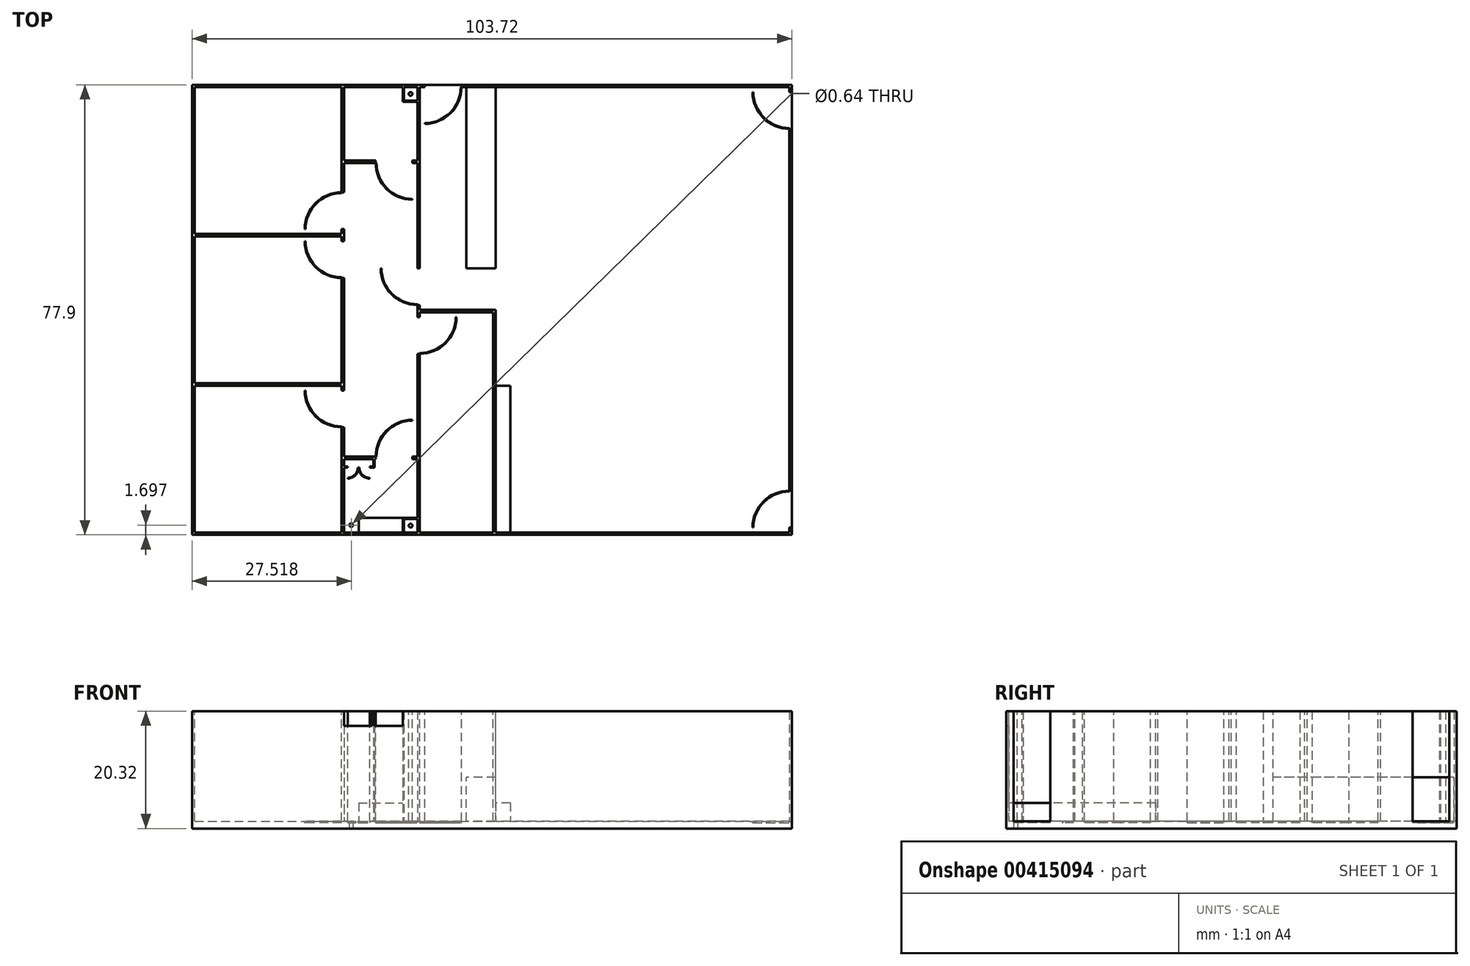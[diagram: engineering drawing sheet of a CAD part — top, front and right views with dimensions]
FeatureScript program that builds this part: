
annotation { "Feature Type Name" : "Feature", "Feature Type Description" : "" }
export const myFeature = defineFeature(function(context is Context, id is Id, definition is map)
    precondition{}
    {
        {
            var Q0;
            Q0=qCreatedBy(makeId("Top.planeOp"),FACE);
            var sketch = newSketch(context, id + "F0", { "sketchPlane" : qUnion([Q0])});
            skLineSegment(sketch, "E0.bottom", {"start": v(51.86, 38.95) * mm, "end": v(-51.86, 38.95) * mm});
            skLineSegment(sketch, "E0.top", {"start": v(51.86, -38.95) * mm, "end": v(-51.86, -38.95) * mm});
            skLineSegment(sketch, "E0.left", {"start": v(51.86, 38.95) * mm, "end": v(51.86, -38.95) * mm});
            skLineSegment(sketch, "E0.right", {"start": v(-51.86, 38.95) * mm, "end": v(-51.86, -38.95) * mm});
            skPoint(sketch, "E0.middle", {"position": v(0, 0) * mm});
            skSolve(sketch);
        }
        {
            var Q0;
            Q0 = qSketchRegion(id + "F0", true);
            extrude(context, id + "F1", {"entities" : qUnion([Q0]), "depth" : 20.32 * mm});
        }
        {
            var Q0;
            Q0=makeQuery(id+"F1.opExtrude","CAP_FACE",FACE,{"disambiguationData":[OSD([sQuery(id+"F0.wireOp",EDGE,"E0.bottom"),sQuery(id+"F0.wireOp",EDGE,"E0.top"),sQuery(id+"F0.wireOp",EDGE,"E0.left"),sQuery(id+"F0.wireOp",EDGE,"E0.right")])],"isStart":false});
            var sketch = newSketch(context, id + "F2", { "sketchPlane" : qUnion([Q0])});
            skLineSegment(sketch, "E1.bottom", {"start": v(-51.43, 38.52) * mm, "end": v(-26.03, 38.52) * mm});
            skLineSegment(sketch, "E1.top", {"start": v(-51.43, 13.12) * mm, "end": v(-26.03, 13.12) * mm});
            skLineSegment(sketch, "E1.left", {"start": v(-51.43, 38.52) * mm, "end": v(-51.43, 13.12) * mm});
            skLineSegment(sketch, "E1.right", {"start": v(-26.03, 38.52) * mm, "end": v(-26.03, 13.12) * mm});
            skLineSegment(sketch, "E2.bottom", {"start": v(-51.43, 12.7) * mm, "end": v(-26.03, 12.7) * mm});
            skLineSegment(sketch, "E2.top", {"start": v(-51.43, -12.7) * mm, "end": v(-26.03, -12.7) * mm});
            skLineSegment(sketch, "E2.left", {"start": v(-51.43, 12.7) * mm, "end": v(-51.43, -12.7) * mm});
            skLineSegment(sketch, "E2.right", {"start": v(-26.03, 12.7) * mm, "end": v(-26.03, -12.7) * mm});
            skLineSegment(sketch, "E3.bottom", {"start": v(-51.43, -13.12) * mm, "end": v(-26.03, -13.12) * mm});
            skLineSegment(sketch, "E3.top", {"start": v(-51.43, -38.52) * mm, "end": v(-26.03, -38.52) * mm});
            skLineSegment(sketch, "E3.left", {"start": v(-51.43, -13.12) * mm, "end": v(-51.43, -38.52) * mm});
            skLineSegment(sketch, "E3.right", {"start": v(-26.03, -13.12) * mm, "end": v(-26.03, -38.52) * mm});
            skLineSegment(sketch, "E4.bottom", {"start": v(-25.61, -25.82) * mm, "end": v(-12.91, -25.82) * mm});
            skLineSegment(sketch, "E4.top", {"start": v(-25.61, -38.52) * mm, "end": v(-12.91, -38.52) * mm});
            skLineSegment(sketch, "E4.left", {"start": v(-25.61, -25.82) * mm, "end": v(-25.61, -38.52) * mm});
            skLineSegment(sketch, "E4.right", {"start": v(-12.91, -25.82) * mm, "end": v(-12.91, -38.52) * mm});
            skLineSegment(sketch, "E5.bottom", {"start": v(-25.61, 38.52) * mm, "end": v(-12.91, 38.52) * mm});
            skLineSegment(sketch, "E5.top", {"start": v(-25.61, 25.82) * mm, "end": v(-12.91, 25.82) * mm});
            skLineSegment(sketch, "E5.left", {"start": v(-25.61, 38.52) * mm, "end": v(-25.61, 25.82) * mm});
            skLineSegment(sketch, "E5.right", {"start": v(-12.91, 38.52) * mm, "end": v(-12.91, 25.82) * mm});
            skLineSegment(sketch, "E6", {"start": v(-25.61, 25.82) * mm, "end": v(-25.61, -25.82) * mm});
            skLineSegment(sketch, "E7.bottom", {"start": v(-12.49, 0) * mm, "end": v(0.64, 0) * mm});
            skLineSegment(sketch, "E7.top", {"start": v(-12.49, -38.52) * mm, "end": v(0.64, -38.52) * mm});
            skLineSegment(sketch, "E7.left", {"start": v(-12.49, 0) * mm, "end": v(-12.49, -38.52) * mm});
            skLineSegment(sketch, "E7.right", {"start": v(0.64, 0) * mm, "end": v(0.64, -38.52) * mm});
            skLineSegment(sketch, "E8", {"start": v(-12.49, 38.52) * mm, "end": v(-12.49, 7.2) * mm});
            skLineSegment(sketch, "E9", {"start": v(-12.91, 25.82) * mm, "end": v(-12.91, 7.2) * mm});
            skLineSegment(sketch, "E10", {"start": v(-12.91, 7.2) * mm, "end": v(-12.49, 7.2) * mm});
            skLineSegment(sketch, "E11", {"start": v(-12.91, -25.82) * mm, "end": v(-12.91, 0) * mm});
            skLineSegment(sketch, "E12", {"start": v(-12.91, 0) * mm, "end": v(-12.49, 0) * mm});
            skLineSegment(sketch, "E13.bottom", {"start": v(0.64, 38.52) * mm, "end": v(-4.44, 38.52) * mm});
            skLineSegment(sketch, "E13.top", {"start": v(0.64, 7.2) * mm, "end": v(-4.44, 7.2) * mm});
            skLineSegment(sketch, "E13.left", {"start": v(0.64, 38.52) * mm, "end": v(0.64, 7.2) * mm});
            skLineSegment(sketch, "E13.right", {"start": v(-4.44, 38.52) * mm, "end": v(-4.44, 7.2) * mm});
            skLineSegment(sketch, "E14", {"start": v(-12.49, 38.52) * mm, "end": v(51.43, 38.52) * mm});
            skLineSegment(sketch, "E15", {"start": v(-25.61, 25.4) * mm, "end": v(-12.91, 25.4) * mm});
            skLineSegment(sketch, "E16", {"start": v(-25.61, -25.4) * mm, "end": v(-12.91, -25.4) * mm});
            skLineSegment(sketch, "E17", {"start": v(-12.49, -0.42) * mm, "end": v(0.21, -0.42) * mm});
            skLineSegment(sketch, "E18", {"start": v(0.21, -0.42) * mm, "end": v(0.21, -38.52) * mm});
            skLineSegment(sketch, "E19", {"start": v(51.43, 38.52) * mm, "end": v(51.43, -38.52) * mm});
            skLineSegment(sketch, "E20", {"start": v(51.43, -38.52) * mm, "end": v(0.64, -38.52) * mm});
            skLineSegment(sketch, "E21", {"start": v(-12.91, 0.85) * mm, "end": v(-12.49, 0.85) * mm});
            skLineSegment(sketch, "E22", {"start": v(-12.49, 0.85) * mm, "end": v(-12.49, 0) * mm});
            skLineSegment(sketch, "E23", {"start": v(-12.91, 0.85) * mm, "end": v(-12.91, 0) * mm});
            skSolve(sketch);
        }
        {
            var Q0;
            Q0=makeQuery(id+"F2.imprint","IMPRINT",FACE,{"disambiguationData":[TD([[makeQuery(id+"F2.imprint","IMPRINT",EDGE,{"derivedFrom":sQuery(id+"F2.wireOp",EDGE,"E7.bottom")}),1.0]])]});
            var Q1;
            {var subQ4=sQuery(id+"F2.wireOp",EDGE,"E17");Q1=makeQuery(id+"F2.imprint","IMPRINT",FACE,{"disambiguationData":[TD([[makeQuery(id+"F2.imprint","IMPRINT",EDGE,{"derivedFrom":subQ4}),-1.0]])]});}
            var Q2;
            Q2=makeQuery(id+"F2.imprint","IMPRINT",FACE,{"disambiguationData":[TD([[makeQuery(id+"F2.imprint","IMPRINT",EDGE,{"derivedFrom":sQuery(id+"F2.wireOp",EDGE,"E5.bottom")}),-1.0]])]});
            var Q3;
            Q3=makeQuery(id+"F2.imprint","IMPRINT",FACE,{"disambiguationData":[TD([[makeQuery(id+"F2.imprint","IMPRINT",EDGE,{"derivedFrom":sQuery(id+"F2.wireOp",EDGE,"E1.bottom")}),-1.0]])]});
            var Q4;
            Q4=makeQuery(id+"F2.imprint","IMPRINT",FACE,{"disambiguationData":[TD([[makeQuery(id+"F2.imprint","IMPRINT",EDGE,{"derivedFrom":sQuery(id+"F2.wireOp",EDGE,"E2.bottom")}),-1.0]])]});
            var Q5;
            Q5=makeQuery(id+"F2.imprint","IMPRINT",FACE,{"disambiguationData":[TD([[makeQuery(id+"F2.imprint","IMPRINT",EDGE,{"derivedFrom":sQuery(id+"F2.wireOp",EDGE,"E3.bottom")}),-1.0]])]});
            var Q6;
            Q6=makeQuery(id+"F2.imprint","IMPRINT",FACE,{"disambiguationData":[TD([[makeQuery(id+"F2.imprint","IMPRINT",EDGE,{"derivedFrom":sQuery(id+"F2.wireOp",EDGE,"E4.bottom")}),-1.0]])]});
            extrude(context, id + "F3", {"entities" : qUnion([Q0, Q1, Q2, Q3, Q4, Q5, Q6]), "operationType" : NewBodyOperationType.REMOVE, "oppositeDirection" : true, "depth" : 19.05 * mm});
        }
        {
            var Q0;
            Q0=makeQuery(id+"F2.imprint","IMPRINT",FACE,{"disambiguationData":[TD([[makeQuery(id+"F2.imprint","IMPRINT",EDGE,{"derivedFrom":sQuery(id+"F2.wireOp",EDGE,"E13.top")}),-1.0]])]});
            extrude(context, id + "F4", {"entities" : qUnion([Q0]), "operationType" : NewBodyOperationType.REMOVE, "oppositeDirection" : true, "depth" : 11.43 * mm});
        }
        {
            var Q0;
            Q0=makeQuery(id+"F3.boolean.opBoolean","COPY",FACE,{"derivedFrom":makeQuery(id+"F3.opExtrude","CAP_FACE",FACE,{"disambiguationData":[OSD([sQuery(id+"F2.wireOp",EDGE,"E6"),sQuery(id+"F2.wireOp",EDGE,"E7.bottom"),sQuery(id+"F2.wireOp",EDGE,"E7.right"),sQuery(id+"F2.wireOp",EDGE,"E8"),sQuery(id+"F2.wireOp",EDGE,"E9"),sQuery(id+"F2.wireOp",EDGE,"E10"),sQuery(id+"F2.wireOp",EDGE,"E11"),sQuery(id+"F2.wireOp",EDGE,"E12"),sQuery(id+"F2.wireOp",EDGE,"E13.top"),sQuery(id+"F2.wireOp",EDGE,"E13.left"),sQuery(id+"F2.wireOp",EDGE,"E13.right"),sQuery(id+"F2.wireOp",EDGE,"E14"),sQuery(id+"F2.wireOp",EDGE,"E15"),sQuery(id+"F2.wireOp",EDGE,"E16"),sQuery(id+"F2.wireOp",EDGE,"E19"),sQuery(id+"F2.wireOp",EDGE,"E20")])],"isStart":false})});
            var sketch = newSketch(context, id + "F5", { "sketchPlane" : qUnion([Q0])});
            skLineSegment(sketch, "E24.bottom", {"start": v(-14.34, -7.62) * mm, "end": v(-3.56, -7.62) * mm});
            skLineSegment(sketch, "E24.top", {"start": v(-14.34, -1.27) * mm, "end": v(-3.56, -1.27) * mm});
            skLineSegment(sketch, "E24.left", {"start": v(-14.34, -7.62) * mm, "end": v(-14.34, -1.27) * mm});
            skLineSegment(sketch, "E24.right", {"start": v(-3.56, -7.62) * mm, "end": v(-3.56, -1.27) * mm});
            skLineSegment(sketch, "E25.bottom", {"start": v(-24.44, -13.97) * mm, "end": v(-32.91, -13.97) * mm});
            skLineSegment(sketch, "E25.top", {"start": v(-24.44, -20.32) * mm, "end": v(-32.91, -20.32) * mm});
            skLineSegment(sketch, "E25.left", {"start": v(-24.44, -13.97) * mm, "end": v(-24.44, -20.32) * mm});
            skLineSegment(sketch, "E25.right", {"start": v(-32.91, -13.97) * mm, "end": v(-32.91, -20.32) * mm});
            skLineSegment(sketch, "E26.bottom", {"start": v(-33.22, 13.97) * mm, "end": v(-23.28, 13.97) * mm});
            skLineSegment(sketch, "E26.top", {"start": v(-33.22, 20.32) * mm, "end": v(-23.28, 20.32) * mm});
            skLineSegment(sketch, "E26.left", {"start": v(-33.22, 13.97) * mm, "end": v(-33.22, 20.32) * mm});
            skLineSegment(sketch, "E26.right", {"start": v(-23.28, 13.97) * mm, "end": v(-23.28, 20.32) * mm});
            skLineSegment(sketch, "E27.bottom", {"start": v(-33.63, 11.85) * mm, "end": v(-25.61, 11.85) * mm});
            skLineSegment(sketch, "E27.top", {"start": v(-33.63, 5.5) * mm, "end": v(-25.61, 5.5) * mm});
            skLineSegment(sketch, "E27.left", {"start": v(-33.63, 11.85) * mm, "end": v(-33.63, 5.5) * mm});
            skLineSegment(sketch, "E27.right", {"start": v(-25.61, 11.85) * mm, "end": v(-25.61, 5.5) * mm});
            skLineSegment(sketch, "E28.bottom", {"start": v(-20.1, 28.26) * mm, "end": v(-13.76, 28.26) * mm});
            skLineSegment(sketch, "E28.top", {"start": v(-20.1, 22.28) * mm, "end": v(-13.76, 22.28) * mm});
            skLineSegment(sketch, "E28.left", {"start": v(-20.1, 28.26) * mm, "end": v(-20.1, 22.28) * mm});
            skLineSegment(sketch, "E28.right", {"start": v(-13.76, 28.26) * mm, "end": v(-13.76, 22.28) * mm});
            skLineSegment(sketch, "E29.bottom", {"start": v(-20.1, -22.33) * mm, "end": v(-13.76, -22.33) * mm});
            skLineSegment(sketch, "E29.top", {"start": v(-20.1, -29.4) * mm, "end": v(-13.76, -29.4) * mm});
            skLineSegment(sketch, "E29.left", {"start": v(-20.1, -22.33) * mm, "end": v(-20.1, -29.4) * mm});
            skLineSegment(sketch, "E29.right", {"start": v(-13.76, -22.33) * mm, "end": v(-13.76, -29.4) * mm});
            skLineSegment(sketch, "E30.bottom", {"start": v(41.47, 37.68) * mm, "end": v(56, 37.68) * mm});
            skLineSegment(sketch, "E30.top", {"start": v(41.47, 31.33) * mm, "end": v(56, 31.33) * mm});
            skLineSegment(sketch, "E30.left", {"start": v(41.47, 37.68) * mm, "end": v(41.47, 31.33) * mm});
            skLineSegment(sketch, "E30.right", {"start": v(56, 37.68) * mm, "end": v(56, 31.33) * mm});
            skLineSegment(sketch, "E31.bottom", {"start": v(42.78, -31.33) * mm, "end": v(59.87, -31.33) * mm});
            skLineSegment(sketch, "E31.top", {"start": v(42.78, -37.68) * mm, "end": v(59.87, -37.68) * mm});
            skLineSegment(sketch, "E31.left", {"start": v(42.78, -31.33) * mm, "end": v(42.78, -37.68) * mm});
            skLineSegment(sketch, "E31.right", {"start": v(59.87, -31.33) * mm, "end": v(59.87, -37.68) * mm});
            skSolve(sketch);
        }
        {
            var Q0;
            Q0 = qSketchRegion(id + "F5", true);
            extrude(context, id + "F6", {"entities" : qUnion([Q0]), "operationType" : NewBodyOperationType.REMOVE, "depth" : 25.4 * mm});
        }
        {
            var Q0;
            Q0=makeQuery(id+"F6.boolean.opBoolean","MERGE",FACE,{"derivedFrom":[makeQuery(id+"F3.boolean.opBoolean","COPY",FACE,{"derivedFrom":makeQuery(id+"F3.opExtrude","CAP_FACE",FACE,{"disambiguationData":[OSD([sQuery(id+"F2.wireOp",EDGE,"E1.bottom"),sQuery(id+"F2.wireOp",EDGE,"E1.top"),sQuery(id+"F2.wireOp",EDGE,"E1.left"),sQuery(id+"F2.wireOp",EDGE,"E1.right")])],"isStart":false})}),makeQuery(id+"F3.boolean.opBoolean","COPY",FACE,{"derivedFrom":makeQuery(id+"F3.opExtrude","CAP_FACE",FACE,{"disambiguationData":[OSD([sQuery(id+"F2.wireOp",EDGE,"E2.bottom"),sQuery(id+"F2.wireOp",EDGE,"E2.top"),sQuery(id+"F2.wireOp",EDGE,"E2.left"),sQuery(id+"F2.wireOp",EDGE,"E2.right")])],"isStart":false})}),makeQuery(id+"F3.boolean.opBoolean","COPY",FACE,{"derivedFrom":makeQuery(id+"F3.opExtrude","CAP_FACE",FACE,{"disambiguationData":[OSD([sQuery(id+"F2.wireOp",EDGE,"E3.bottom"),sQuery(id+"F2.wireOp",EDGE,"E3.top"),sQuery(id+"F2.wireOp",EDGE,"E3.left"),sQuery(id+"F2.wireOp",EDGE,"E3.right")])],"isStart":false})}),makeQuery(id+"F3.boolean.opBoolean","COPY",FACE,{"derivedFrom":makeQuery(id+"F3.opExtrude","CAP_FACE",FACE,{"disambiguationData":[OSD([sQuery(id+"F2.wireOp",EDGE,"E4.bottom"),sQuery(id+"F2.wireOp",EDGE,"E4.top"),sQuery(id+"F2.wireOp",EDGE,"E4.left"),sQuery(id+"F2.wireOp",EDGE,"E4.right")])],"isStart":false})}),makeQuery(id+"F3.boolean.opBoolean","COPY",FACE,{"derivedFrom":makeQuery(id+"F3.opExtrude","CAP_FACE",FACE,{"disambiguationData":[OSD([sQuery(id+"F2.wireOp",EDGE,"E5.bottom"),sQuery(id+"F2.wireOp",EDGE,"E5.top"),sQuery(id+"F2.wireOp",EDGE,"E5.left"),sQuery(id+"F2.wireOp",EDGE,"E5.right")])],"isStart":false})}),makeQuery(id+"F3.boolean.opBoolean","COPY",FACE,{"derivedFrom":makeQuery(id+"F3.opExtrude","CAP_FACE",FACE,{"disambiguationData":[OSD([sQuery(id+"F2.wireOp",EDGE,"E6"),sQuery(id+"F2.wireOp",EDGE,"E7.bottom"),sQuery(id+"F2.wireOp",EDGE,"E7.right"),sQuery(id+"F2.wireOp",EDGE,"E8"),sQuery(id+"F2.wireOp",EDGE,"E9"),sQuery(id+"F2.wireOp",EDGE,"E10"),sQuery(id+"F2.wireOp",EDGE,"E11"),sQuery(id+"F2.wireOp",EDGE,"E13.top"),sQuery(id+"F2.wireOp",EDGE,"E13.left"),sQuery(id+"F2.wireOp",EDGE,"E13.right"),sQuery(id+"F2.wireOp",EDGE,"E14"),sQuery(id+"F2.wireOp",EDGE,"E15"),sQuery(id+"F2.wireOp",EDGE,"E16"),sQuery(id+"F2.wireOp",EDGE,"E19"),sQuery(id+"F2.wireOp",EDGE,"E20"),sQuery(id+"F2.wireOp",EDGE,"E21"),sQuery(id+"F2.wireOp",EDGE,"E22"),sQuery(id+"F2.wireOp",EDGE,"E23")])],"isStart":false})}),makeQuery(id+"F3.boolean.opBoolean","COPY",FACE,{"derivedFrom":makeQuery(id+"F3.opExtrude","CAP_FACE",FACE,{"disambiguationData":[OSD([sQuery(id+"F2.wireOp",EDGE,"E7.top"),sQuery(id+"F2.wireOp",EDGE,"E7.left"),sQuery(id+"F2.wireOp",EDGE,"E17"),sQuery(id+"F2.wireOp",EDGE,"E18")])],"isStart":false})}),makeQuery(id+"F6.opExtrude","CAP_FACE",FACE,{"disambiguationData":[OSD([sQuery(id+"F5.wireOp",EDGE,"E24.bottom"),sQuery(id+"F5.wireOp",EDGE,"E24.top"),sQuery(id+"F5.wireOp",EDGE,"E24.left"),sQuery(id+"F5.wireOp",EDGE,"E24.right")])],"isStart":true}),makeQuery(id+"F6.opExtrude","CAP_FACE",FACE,{"disambiguationData":[OSD([sQuery(id+"F5.wireOp",EDGE,"E25.bottom"),sQuery(id+"F5.wireOp",EDGE,"E25.top"),sQuery(id+"F5.wireOp",EDGE,"E25.left"),sQuery(id+"F5.wireOp",EDGE,"E25.right")])],"isStart":true}),makeQuery(id+"F6.opExtrude","CAP_FACE",FACE,{"disambiguationData":[OSD([sQuery(id+"F5.wireOp",EDGE,"E26.bottom"),sQuery(id+"F5.wireOp",EDGE,"E26.top"),sQuery(id+"F5.wireOp",EDGE,"E26.left"),sQuery(id+"F5.wireOp",EDGE,"E26.right")])],"isStart":true}),makeQuery(id+"F6.opExtrude","CAP_FACE",FACE,{"disambiguationData":[OSD([sQuery(id+"F5.wireOp",EDGE,"E27.bottom"),sQuery(id+"F5.wireOp",EDGE,"E27.top"),sQuery(id+"F5.wireOp",EDGE,"E27.left"),sQuery(id+"F5.wireOp",EDGE,"E27.right")])],"isStart":true}),makeQuery(id+"F6.opExtrude","CAP_FACE",FACE,{"disambiguationData":[OSD([sQuery(id+"F5.wireOp",EDGE,"E28.bottom"),sQuery(id+"F5.wireOp",EDGE,"E28.top"),sQuery(id+"F5.wireOp",EDGE,"E28.left"),sQuery(id+"F5.wireOp",EDGE,"E28.right")])],"isStart":true}),makeQuery(id+"F6.opExtrude","CAP_FACE",FACE,{"disambiguationData":[OSD([sQuery(id+"F5.wireOp",EDGE,"E29.bottom"),sQuery(id+"F5.wireOp",EDGE,"E29.top"),sQuery(id+"F5.wireOp",EDGE,"E29.left"),sQuery(id+"F5.wireOp",EDGE,"E29.right")])],"isStart":true})]});
            var sketch = newSketch(context, id + "F7", { "sketchPlane" : qUnion([Q0])});
            skArc(sketch, "E32", {"start": v(-20.1, -25.4) * mm, "mid": v(-18.25, -20.9) * mm, "end": v(-13.76, -19.05) * mm});
            skArc(sketch, "E33", {"start": v(-26.03, -20.32) * mm, "mid": v(-30.53, -18.46) * mm, "end": v(-32.38, -13.97) * mm});
            skArc(sketch, "E34", {"start": v(-12.49, -7.62) * mm, "mid": v(-8, -5.76) * mm, "end": v(-6.14, -1.27) * mm});
            skArc(sketch, "E35", {"start": v(-26.03, 5.5) * mm, "mid": v(-30.53, 7.36) * mm, "end": v(-32.38, 11.85) * mm});
            skArc(sketch, "E36", {"start": v(-26.03, 20.32) * mm, "mid": v(-30.53, 18.46) * mm, "end": v(-32.38, 13.97) * mm});
            skArc(sketch, "E37", {"start": v(-20.1, 25.4) * mm, "mid": v(-18.25, 20.9) * mm, "end": v(-13.76, 19.05) * mm});
            skArc(sketch, "E38", {"start": v(-12.91, 0.85) * mm, "mid": v(-17.4, 2.7) * mm, "end": v(-19.26, 7.2) * mm});
            skArc(sketch, "E39", {"start": v(-19.98, -25.4) * mm, "mid": v(-18.16, -21) * mm, "end": v(-13.76, -19.18) * mm});
            skArc(sketch, "E40", {"start": v(-26.03, -20.2) * mm, "mid": v(-30.44, -18.37) * mm, "end": v(-32.26, -13.97) * mm});
            skArc(sketch, "E41", {"start": v(-12.49, -7.5) * mm, "mid": v(-8.09, -5.67) * mm, "end": v(-6.27, -1.27) * mm});
            skArc(sketch, "E42", {"start": v(-12.91, 0.97) * mm, "mid": v(-17.31, 2.8) * mm, "end": v(-19.13, 7.2) * mm});
            skArc(sketch, "E43", {"start": v(-26.03, 5.63) * mm, "mid": v(-30.44, 7.45) * mm, "end": v(-32.26, 11.85) * mm});
            skArc(sketch, "E44", {"start": v(-26.03, 20.2) * mm, "mid": v(-30.44, 18.37) * mm, "end": v(-32.26, 13.97) * mm});
            skArc(sketch, "E45", {"start": v(-19.98, 25.4) * mm, "mid": v(-18.16, 21) * mm, "end": v(-13.76, 19.18) * mm});
            skLineSegment(sketch, "E46", {"start": v(-13.76, -19.18) * mm, "end": v(-13.76, -19.18) * mm});
            skLineSegment(sketch, "E47", {"start": v(-13.76, -19.18) * mm, "end": v(-13.76, -19.05) * mm});
            skLineSegment(sketch, "E48", {"start": v(-19.98, -25.4) * mm, "end": v(-20.1, -25.4) * mm});
            skLineSegment(sketch, "E49", {"start": v(-26.03, -20.2) * mm, "end": v(-26.03, -20.32) * mm});
            skLineSegment(sketch, "E50", {"start": v(-32.26, -13.97) * mm, "end": v(-32.38, -13.97) * mm});
            skLineSegment(sketch, "E51", {"start": v(-6.14, -1.27) * mm, "end": v(-6.27, -1.27) * mm});
            skLineSegment(sketch, "E52", {"start": v(-12.49, -7.62) * mm, "end": v(-12.49, -7.5) * mm});
            skLineSegment(sketch, "E53", {"start": v(-12.91, 0.97) * mm, "end": v(-12.91, 0.85) * mm});
            skLineSegment(sketch, "E54", {"start": v(-19.26, 7.2) * mm, "end": v(-19.13, 7.2) * mm});
            skLineSegment(sketch, "E55", {"start": v(-26.03, 5.5) * mm, "end": v(-26.03, 5.63) * mm});
            skLineSegment(sketch, "E56", {"start": v(-32.38, 11.85) * mm, "end": v(-32.26, 11.85) * mm});
            skLineSegment(sketch, "E57", {"start": v(-32.38, 13.97) * mm, "end": v(-32.26, 13.97) * mm});
            skLineSegment(sketch, "E58", {"start": v(-26.03, 20.2) * mm, "end": v(-26.03, 20.32) * mm});
            skLineSegment(sketch, "E59", {"start": v(-13.76, 19.05) * mm, "end": v(-13.76, 19.18) * mm});
            skLineSegment(sketch, "E60", {"start": v(-20.1, 25.4) * mm, "end": v(-19.98, 25.4) * mm});
            skSolve(sketch);
        }
        {
            var Q0;
            Q0 = qSketchRegion(id + "F7", true);
            extrude(context, id + "F8", {"entities" : qUnion([Q0]), "operationType" : NewBodyOperationType.REMOVE, "oppositeDirection" : true, "depth" : 0.25 * mm});
        }
        {
            var Q0;
            Q0=makeQuery(id+"F6.boolean.opBoolean","MERGE",FACE,{"derivedFrom":[makeQuery(id+"F3.boolean.opBoolean","COPY",FACE,{"derivedFrom":makeQuery(id+"F3.opExtrude","CAP_FACE",FACE,{"disambiguationData":[OSD([sQuery(id+"F2.wireOp",EDGE,"E1.bottom"),sQuery(id+"F2.wireOp",EDGE,"E1.top"),sQuery(id+"F2.wireOp",EDGE,"E1.left"),sQuery(id+"F2.wireOp",EDGE,"E1.right")])],"isStart":false})}),makeQuery(id+"F3.boolean.opBoolean","COPY",FACE,{"derivedFrom":makeQuery(id+"F3.opExtrude","CAP_FACE",FACE,{"disambiguationData":[OSD([sQuery(id+"F2.wireOp",EDGE,"E2.bottom"),sQuery(id+"F2.wireOp",EDGE,"E2.top"),sQuery(id+"F2.wireOp",EDGE,"E2.left"),sQuery(id+"F2.wireOp",EDGE,"E2.right")])],"isStart":false})}),makeQuery(id+"F3.boolean.opBoolean","COPY",FACE,{"derivedFrom":makeQuery(id+"F3.opExtrude","CAP_FACE",FACE,{"disambiguationData":[OSD([sQuery(id+"F2.wireOp",EDGE,"E3.bottom"),sQuery(id+"F2.wireOp",EDGE,"E3.top"),sQuery(id+"F2.wireOp",EDGE,"E3.left"),sQuery(id+"F2.wireOp",EDGE,"E3.right")])],"isStart":false})}),makeQuery(id+"F3.boolean.opBoolean","COPY",FACE,{"derivedFrom":makeQuery(id+"F3.opExtrude","CAP_FACE",FACE,{"disambiguationData":[OSD([sQuery(id+"F2.wireOp",EDGE,"E4.bottom"),sQuery(id+"F2.wireOp",EDGE,"E4.top"),sQuery(id+"F2.wireOp",EDGE,"E4.left"),sQuery(id+"F2.wireOp",EDGE,"E4.right")])],"isStart":false})}),makeQuery(id+"F3.boolean.opBoolean","COPY",FACE,{"derivedFrom":makeQuery(id+"F3.opExtrude","CAP_FACE",FACE,{"disambiguationData":[OSD([sQuery(id+"F2.wireOp",EDGE,"E5.bottom"),sQuery(id+"F2.wireOp",EDGE,"E5.top"),sQuery(id+"F2.wireOp",EDGE,"E5.left"),sQuery(id+"F2.wireOp",EDGE,"E5.right")])],"isStart":false})}),makeQuery(id+"F3.boolean.opBoolean","COPY",FACE,{"derivedFrom":makeQuery(id+"F3.opExtrude","CAP_FACE",FACE,{"disambiguationData":[OSD([sQuery(id+"F2.wireOp",EDGE,"E6"),sQuery(id+"F2.wireOp",EDGE,"E7.bottom"),sQuery(id+"F2.wireOp",EDGE,"E7.right"),sQuery(id+"F2.wireOp",EDGE,"E8"),sQuery(id+"F2.wireOp",EDGE,"E9"),sQuery(id+"F2.wireOp",EDGE,"E10"),sQuery(id+"F2.wireOp",EDGE,"E11"),sQuery(id+"F2.wireOp",EDGE,"E13.top"),sQuery(id+"F2.wireOp",EDGE,"E13.left"),sQuery(id+"F2.wireOp",EDGE,"E13.right"),sQuery(id+"F2.wireOp",EDGE,"E14"),sQuery(id+"F2.wireOp",EDGE,"E15"),sQuery(id+"F2.wireOp",EDGE,"E16"),sQuery(id+"F2.wireOp",EDGE,"E19"),sQuery(id+"F2.wireOp",EDGE,"E20"),sQuery(id+"F2.wireOp",EDGE,"E21"),sQuery(id+"F2.wireOp",EDGE,"E22"),sQuery(id+"F2.wireOp",EDGE,"E23")])],"isStart":false})}),makeQuery(id+"F3.boolean.opBoolean","COPY",FACE,{"derivedFrom":makeQuery(id+"F3.opExtrude","CAP_FACE",FACE,{"disambiguationData":[OSD([sQuery(id+"F2.wireOp",EDGE,"E7.top"),sQuery(id+"F2.wireOp",EDGE,"E7.left"),sQuery(id+"F2.wireOp",EDGE,"E17"),sQuery(id+"F2.wireOp",EDGE,"E18")])],"isStart":false})}),makeQuery(id+"F6.opExtrude","CAP_FACE",FACE,{"disambiguationData":[OSD([sQuery(id+"F5.wireOp",EDGE,"E24.bottom"),sQuery(id+"F5.wireOp",EDGE,"E24.top"),sQuery(id+"F5.wireOp",EDGE,"E24.left"),sQuery(id+"F5.wireOp",EDGE,"E24.right")])],"isStart":true}),makeQuery(id+"F6.opExtrude","CAP_FACE",FACE,{"disambiguationData":[OSD([sQuery(id+"F5.wireOp",EDGE,"E25.bottom"),sQuery(id+"F5.wireOp",EDGE,"E25.top"),sQuery(id+"F5.wireOp",EDGE,"E25.left"),sQuery(id+"F5.wireOp",EDGE,"E25.right")])],"isStart":true}),makeQuery(id+"F6.opExtrude","CAP_FACE",FACE,{"disambiguationData":[OSD([sQuery(id+"F5.wireOp",EDGE,"E26.bottom"),sQuery(id+"F5.wireOp",EDGE,"E26.top"),sQuery(id+"F5.wireOp",EDGE,"E26.left"),sQuery(id+"F5.wireOp",EDGE,"E26.right")])],"isStart":true}),makeQuery(id+"F6.opExtrude","CAP_FACE",FACE,{"disambiguationData":[OSD([sQuery(id+"F5.wireOp",EDGE,"E27.bottom"),sQuery(id+"F5.wireOp",EDGE,"E27.top"),sQuery(id+"F5.wireOp",EDGE,"E27.left"),sQuery(id+"F5.wireOp",EDGE,"E27.right")])],"isStart":true}),makeQuery(id+"F6.opExtrude","CAP_FACE",FACE,{"disambiguationData":[OSD([sQuery(id+"F5.wireOp",EDGE,"E28.bottom"),sQuery(id+"F5.wireOp",EDGE,"E28.top"),sQuery(id+"F5.wireOp",EDGE,"E28.left"),sQuery(id+"F5.wireOp",EDGE,"E28.right")])],"isStart":true}),makeQuery(id+"F6.opExtrude","CAP_FACE",FACE,{"disambiguationData":[OSD([sQuery(id+"F5.wireOp",EDGE,"E29.bottom"),sQuery(id+"F5.wireOp",EDGE,"E29.top"),sQuery(id+"F5.wireOp",EDGE,"E29.left"),sQuery(id+"F5.wireOp",EDGE,"E29.right")])],"isStart":true})]});
            var sketch = newSketch(context, id + "F9", { "sketchPlane" : qUnion([Q0])});
            skLineSegment(sketch, "E61.bottom", {"start": v(-23.07, -35.98) * mm, "end": v(-12.91, -35.98) * mm});
            skLineSegment(sketch, "E61.top", {"start": v(-23.07, -38.52) * mm, "end": v(-12.91, -38.52) * mm});
            skLineSegment(sketch, "E61.left", {"start": v(-12.91, -35.98) * mm, "end": v(-12.91, -38.52) * mm});
            skLineSegment(sketch, "E61.right", {"start": v(-23.07, -35.98) * mm, "end": v(-23.07, -38.52) * mm});
            skLineSegment(sketch, "E62.bottom", {"start": v(3.18, -13.12) * mm, "end": v(0.64, -13.12) * mm});
            skLineSegment(sketch, "E62.top", {"start": v(3.18, -38.52) * mm, "end": v(0.64, -38.52) * mm});
            skLineSegment(sketch, "E62.left", {"start": v(3.18, -13.12) * mm, "end": v(3.18, -38.52) * mm});
            skLineSegment(sketch, "E62.right", {"start": v(0.64, -13.12) * mm, "end": v(0.64, -38.52) * mm});
            skLineSegment(sketch, "E63", {"start": v(-15.45, -35.98) * mm, "end": v(-15.45, -38.52) * mm});
            skSolve(sketch);
        }
        {
            var Q0;
            {var subQ0=sQuery(id+"F9.wireOp",EDGE,"E61.right");Q0=makeQuery(id+"F9.imprint","IMPRINT",FACE,{"disambiguationData":[TD([[makeQuery(id+"F9.imprint","IMPRINT",EDGE,{"derivedFrom":subQ0}),1.0]])]});}
            var Q1;
            Q1=makeQuery(id+"F9.imprint","IMPRINT",FACE,{"disambiguationData":[TD([[makeQuery(id+"F9.imprint","IMPRINT",EDGE,{"derivedFrom":sQuery(id+"F9.wireOp",EDGE,"E62.bottom")}),1.0]])]});
            extrude(context, id + "F10", {"entities" : qUnion([Q0, Q1]), "operationType" : NewBodyOperationType.ADD, "depth" : 3.17 * mm});
        }
        {
            var Q0;
            {var subQ0=sQuery(id+"F9.wireOp",EDGE,"E61.left");Q0=makeQuery(id+"F9.imprint","IMPRINT",FACE,{"disambiguationData":[TD([[makeQuery(id+"F9.imprint","IMPRINT",EDGE,{"derivedFrom":subQ0}),-1.0]])]});}
            extrude(context, id + "F11", {"entities" : qUnion([Q0]), "operationType" : NewBodyOperationType.ADD, "depth" : 19.05 * mm});
        }
        {
            var Q0;
            Q0=makeQuery(id+"F6.boolean.opBoolean","MERGE",FACE,{"derivedFrom":[makeQuery(id+"F3.boolean.opBoolean","COPY",FACE,{"derivedFrom":makeQuery(id+"F3.opExtrude","CAP_FACE",FACE,{"disambiguationData":[OSD([sQuery(id+"F2.wireOp",EDGE,"E1.bottom"),sQuery(id+"F2.wireOp",EDGE,"E1.top"),sQuery(id+"F2.wireOp",EDGE,"E1.left"),sQuery(id+"F2.wireOp",EDGE,"E1.right")])],"isStart":false})}),makeQuery(id+"F3.boolean.opBoolean","COPY",FACE,{"derivedFrom":makeQuery(id+"F3.opExtrude","CAP_FACE",FACE,{"disambiguationData":[OSD([sQuery(id+"F2.wireOp",EDGE,"E2.bottom"),sQuery(id+"F2.wireOp",EDGE,"E2.top"),sQuery(id+"F2.wireOp",EDGE,"E2.left"),sQuery(id+"F2.wireOp",EDGE,"E2.right")])],"isStart":false})}),makeQuery(id+"F3.boolean.opBoolean","COPY",FACE,{"derivedFrom":makeQuery(id+"F3.opExtrude","CAP_FACE",FACE,{"disambiguationData":[OSD([sQuery(id+"F2.wireOp",EDGE,"E3.bottom"),sQuery(id+"F2.wireOp",EDGE,"E3.top"),sQuery(id+"F2.wireOp",EDGE,"E3.left"),sQuery(id+"F2.wireOp",EDGE,"E3.right")])],"isStart":false})}),makeQuery(id+"F3.boolean.opBoolean","COPY",FACE,{"derivedFrom":makeQuery(id+"F3.opExtrude","CAP_FACE",FACE,{"disambiguationData":[OSD([sQuery(id+"F2.wireOp",EDGE,"E4.bottom"),sQuery(id+"F2.wireOp",EDGE,"E4.top"),sQuery(id+"F2.wireOp",EDGE,"E4.left"),sQuery(id+"F2.wireOp",EDGE,"E4.right")])],"isStart":false})}),makeQuery(id+"F3.boolean.opBoolean","COPY",FACE,{"derivedFrom":makeQuery(id+"F3.opExtrude","CAP_FACE",FACE,{"disambiguationData":[OSD([sQuery(id+"F2.wireOp",EDGE,"E5.bottom"),sQuery(id+"F2.wireOp",EDGE,"E5.top"),sQuery(id+"F2.wireOp",EDGE,"E5.left"),sQuery(id+"F2.wireOp",EDGE,"E5.right")])],"isStart":false})}),makeQuery(id+"F3.boolean.opBoolean","COPY",FACE,{"derivedFrom":makeQuery(id+"F3.opExtrude","CAP_FACE",FACE,{"disambiguationData":[OSD([sQuery(id+"F2.wireOp",EDGE,"E6"),sQuery(id+"F2.wireOp",EDGE,"E7.bottom"),sQuery(id+"F2.wireOp",EDGE,"E7.right"),sQuery(id+"F2.wireOp",EDGE,"E8"),sQuery(id+"F2.wireOp",EDGE,"E9"),sQuery(id+"F2.wireOp",EDGE,"E10"),sQuery(id+"F2.wireOp",EDGE,"E11"),sQuery(id+"F2.wireOp",EDGE,"E13.top"),sQuery(id+"F2.wireOp",EDGE,"E13.left"),sQuery(id+"F2.wireOp",EDGE,"E13.right"),sQuery(id+"F2.wireOp",EDGE,"E14"),sQuery(id+"F2.wireOp",EDGE,"E15"),sQuery(id+"F2.wireOp",EDGE,"E16"),sQuery(id+"F2.wireOp",EDGE,"E19"),sQuery(id+"F2.wireOp",EDGE,"E20"),sQuery(id+"F2.wireOp",EDGE,"E21"),sQuery(id+"F2.wireOp",EDGE,"E22"),sQuery(id+"F2.wireOp",EDGE,"E23")])],"isStart":false})}),makeQuery(id+"F3.boolean.opBoolean","COPY",FACE,{"derivedFrom":makeQuery(id+"F3.opExtrude","CAP_FACE",FACE,{"disambiguationData":[OSD([sQuery(id+"F2.wireOp",EDGE,"E7.top"),sQuery(id+"F2.wireOp",EDGE,"E7.left"),sQuery(id+"F2.wireOp",EDGE,"E17"),sQuery(id+"F2.wireOp",EDGE,"E18")])],"isStart":false})}),makeQuery(id+"F6.opExtrude","CAP_FACE",FACE,{"disambiguationData":[OSD([sQuery(id+"F5.wireOp",EDGE,"E24.bottom"),sQuery(id+"F5.wireOp",EDGE,"E24.top"),sQuery(id+"F5.wireOp",EDGE,"E24.left"),sQuery(id+"F5.wireOp",EDGE,"E24.right")])],"isStart":true}),makeQuery(id+"F6.opExtrude","CAP_FACE",FACE,{"disambiguationData":[OSD([sQuery(id+"F5.wireOp",EDGE,"E25.bottom"),sQuery(id+"F5.wireOp",EDGE,"E25.top"),sQuery(id+"F5.wireOp",EDGE,"E25.left"),sQuery(id+"F5.wireOp",EDGE,"E25.right")])],"isStart":true}),makeQuery(id+"F6.opExtrude","CAP_FACE",FACE,{"disambiguationData":[OSD([sQuery(id+"F5.wireOp",EDGE,"E26.bottom"),sQuery(id+"F5.wireOp",EDGE,"E26.top"),sQuery(id+"F5.wireOp",EDGE,"E26.left"),sQuery(id+"F5.wireOp",EDGE,"E26.right")])],"isStart":true}),makeQuery(id+"F6.opExtrude","CAP_FACE",FACE,{"disambiguationData":[OSD([sQuery(id+"F5.wireOp",EDGE,"E27.bottom"),sQuery(id+"F5.wireOp",EDGE,"E27.top"),sQuery(id+"F5.wireOp",EDGE,"E27.left"),sQuery(id+"F5.wireOp",EDGE,"E27.right")])],"isStart":true}),makeQuery(id+"F6.opExtrude","CAP_FACE",FACE,{"disambiguationData":[OSD([sQuery(id+"F5.wireOp",EDGE,"E28.bottom"),sQuery(id+"F5.wireOp",EDGE,"E28.top"),sQuery(id+"F5.wireOp",EDGE,"E28.left"),sQuery(id+"F5.wireOp",EDGE,"E28.right")])],"isStart":true}),makeQuery(id+"F6.opExtrude","CAP_FACE",FACE,{"disambiguationData":[OSD([sQuery(id+"F5.wireOp",EDGE,"E29.bottom"),sQuery(id+"F5.wireOp",EDGE,"E29.top"),sQuery(id+"F5.wireOp",EDGE,"E29.left"),sQuery(id+"F5.wireOp",EDGE,"E29.right")])],"isStart":true})]});
            var sketch = newSketch(context, id + "F12", { "sketchPlane" : qUnion([Q0])});
            skCircle(sketch, "E64", {"center": v(-24.34, -37.25) * mm, "radius": 0.32 * mm});
            skPoint(sketch, "E64.centerSnap0", {"position": v(-24.34, -38.52) * mm});
            skPoint(sketch, "E64.centerSnap1", {"position": v(-23.07, -37.25) * mm});
            skSolve(sketch);
        }
        {
            var Q0;
            Q0 = qSketchRegion(id + "F12", true);
            extrude(context, id + "F13", {"entities" : qUnion([Q0]), "operationType" : NewBodyOperationType.REMOVE, "oppositeDirection" : true, "depth" : 25.4 * mm});
        }
        {
            var Q0;
            Q0=makeQuery(id+"F11.boolean.opBoolean","MERGE",FACE,{"derivedFrom":[makeQuery(id+"F1.opExtrude","CAP_FACE",FACE,{"disambiguationData":[OSD([sQuery(id+"F0.wireOp",EDGE,"E0.bottom"),sQuery(id+"F0.wireOp",EDGE,"E0.top"),sQuery(id+"F0.wireOp",EDGE,"E0.left"),sQuery(id+"F0.wireOp",EDGE,"E0.right")])],"isStart":false}),makeQuery(id+"F11.opExtrude","CAP_FACE",FACE,{"disambiguationData":[OSD([sQuery(id+"F9.wireOp",EDGE,"E61.bottom"),sQuery(id+"F9.wireOp",EDGE,"E61.top"),sQuery(id+"F9.wireOp",EDGE,"E61.left"),sQuery(id+"F9.wireOp",EDGE,"E63")])],"isStart":false})]});
            var sketch = newSketch(context, id + "F14", { "sketchPlane" : qUnion([Q0])});
            skLineSegment(sketch, "E65.bottom", {"start": v(-15.24, -36.2) * mm, "end": v(-12.91, -36.2) * mm});
            skLineSegment(sketch, "E65.top", {"start": v(-15.24, -38.52) * mm, "end": v(-12.91, -38.52) * mm});
            skLineSegment(sketch, "E65.left", {"start": v(-15.24, -36.2) * mm, "end": v(-15.24, -38.52) * mm});
            skLineSegment(sketch, "E65.right", {"start": v(-12.91, -36.2) * mm, "end": v(-12.91, -38.52) * mm});
            skPoint(sketch, "E65.middle", {"position": v(-14.18, -37.25) * mm});
            skPoint(sketch, "E65.middle.positionSnap0", {"position": v(-15.45, -37.25) * mm});
            skPoint(sketch, "E65.middle.positionSnap1", {"position": v(-14.18, -35.98) * mm});
            skPoint(sketch, "E65.centerSnap0", {"position": v(-15.45, -37.25) * mm});
            skPoint(sketch, "E65.centerSnap1", {"position": v(-14.18, -35.98) * mm});
            skCircle(sketch, "E66", {"center": v(-14.08, -37.36) * mm, "radius": 0.32 * mm});
            skPoint(sketch, "E66.centerSnap0", {"position": v(-14.08, -38.52) * mm});
            skPoint(sketch, "E66.centerSnap1", {"position": v(-12.91, -37.36) * mm});
            skSolve(sketch);
        }
        {
            var Q0;
            Q0=makeQuery(id+"F14.imprint","IMPRINT",FACE,{"disambiguationData":[TD([[makeQuery(id+"F14.imprint","IMPRINT",EDGE,{"derivedFrom":sQuery(id+"F14.wireOp",EDGE,"E65.bottom")}),-1.0]])]});
            extrude(context, id + "F15", {"entities" : qUnion([Q0]), "operationType" : NewBodyOperationType.REMOVE, "oppositeDirection" : true, "depth" : 19.05 * mm});
        }
        {
            var Q0;
            Q0=makeQuery(id+"F6.boolean.opBoolean","MERGE",FACE,{"derivedFrom":[makeQuery(id+"F3.boolean.opBoolean","COPY",FACE,{"derivedFrom":makeQuery(id+"F3.opExtrude","CAP_FACE",FACE,{"disambiguationData":[OSD([sQuery(id+"F2.wireOp",EDGE,"E1.bottom"),sQuery(id+"F2.wireOp",EDGE,"E1.top"),sQuery(id+"F2.wireOp",EDGE,"E1.left"),sQuery(id+"F2.wireOp",EDGE,"E1.right")])],"isStart":false})}),makeQuery(id+"F3.boolean.opBoolean","COPY",FACE,{"derivedFrom":makeQuery(id+"F3.opExtrude","CAP_FACE",FACE,{"disambiguationData":[OSD([sQuery(id+"F2.wireOp",EDGE,"E2.bottom"),sQuery(id+"F2.wireOp",EDGE,"E2.top"),sQuery(id+"F2.wireOp",EDGE,"E2.left"),sQuery(id+"F2.wireOp",EDGE,"E2.right")])],"isStart":false})}),makeQuery(id+"F3.boolean.opBoolean","COPY",FACE,{"derivedFrom":makeQuery(id+"F3.opExtrude","CAP_FACE",FACE,{"disambiguationData":[OSD([sQuery(id+"F2.wireOp",EDGE,"E3.bottom"),sQuery(id+"F2.wireOp",EDGE,"E3.top"),sQuery(id+"F2.wireOp",EDGE,"E3.left"),sQuery(id+"F2.wireOp",EDGE,"E3.right")])],"isStart":false})}),makeQuery(id+"F3.boolean.opBoolean","COPY",FACE,{"derivedFrom":makeQuery(id+"F3.opExtrude","CAP_FACE",FACE,{"disambiguationData":[OSD([sQuery(id+"F2.wireOp",EDGE,"E4.bottom"),sQuery(id+"F2.wireOp",EDGE,"E4.top"),sQuery(id+"F2.wireOp",EDGE,"E4.left"),sQuery(id+"F2.wireOp",EDGE,"E4.right")])],"isStart":false})}),makeQuery(id+"F3.boolean.opBoolean","COPY",FACE,{"derivedFrom":makeQuery(id+"F3.opExtrude","CAP_FACE",FACE,{"disambiguationData":[OSD([sQuery(id+"F2.wireOp",EDGE,"E5.bottom"),sQuery(id+"F2.wireOp",EDGE,"E5.top"),sQuery(id+"F2.wireOp",EDGE,"E5.left"),sQuery(id+"F2.wireOp",EDGE,"E5.right")])],"isStart":false})}),makeQuery(id+"F3.boolean.opBoolean","COPY",FACE,{"derivedFrom":makeQuery(id+"F3.opExtrude","CAP_FACE",FACE,{"disambiguationData":[OSD([sQuery(id+"F2.wireOp",EDGE,"E6"),sQuery(id+"F2.wireOp",EDGE,"E7.bottom"),sQuery(id+"F2.wireOp",EDGE,"E7.right"),sQuery(id+"F2.wireOp",EDGE,"E8"),sQuery(id+"F2.wireOp",EDGE,"E9"),sQuery(id+"F2.wireOp",EDGE,"E10"),sQuery(id+"F2.wireOp",EDGE,"E11"),sQuery(id+"F2.wireOp",EDGE,"E13.top"),sQuery(id+"F2.wireOp",EDGE,"E13.left"),sQuery(id+"F2.wireOp",EDGE,"E13.right"),sQuery(id+"F2.wireOp",EDGE,"E14"),sQuery(id+"F2.wireOp",EDGE,"E15"),sQuery(id+"F2.wireOp",EDGE,"E16"),sQuery(id+"F2.wireOp",EDGE,"E19"),sQuery(id+"F2.wireOp",EDGE,"E20"),sQuery(id+"F2.wireOp",EDGE,"E21"),sQuery(id+"F2.wireOp",EDGE,"E22"),sQuery(id+"F2.wireOp",EDGE,"E23")])],"isStart":false})}),makeQuery(id+"F3.boolean.opBoolean","COPY",FACE,{"derivedFrom":makeQuery(id+"F3.opExtrude","CAP_FACE",FACE,{"disambiguationData":[OSD([sQuery(id+"F2.wireOp",EDGE,"E7.top"),sQuery(id+"F2.wireOp",EDGE,"E7.left"),sQuery(id+"F2.wireOp",EDGE,"E17"),sQuery(id+"F2.wireOp",EDGE,"E18")])],"isStart":false})}),makeQuery(id+"F6.opExtrude","CAP_FACE",FACE,{"disambiguationData":[OSD([sQuery(id+"F5.wireOp",EDGE,"E24.bottom"),sQuery(id+"F5.wireOp",EDGE,"E24.top"),sQuery(id+"F5.wireOp",EDGE,"E24.left"),sQuery(id+"F5.wireOp",EDGE,"E24.right")])],"isStart":true}),makeQuery(id+"F6.opExtrude","CAP_FACE",FACE,{"disambiguationData":[OSD([sQuery(id+"F5.wireOp",EDGE,"E25.bottom"),sQuery(id+"F5.wireOp",EDGE,"E25.top"),sQuery(id+"F5.wireOp",EDGE,"E25.left"),sQuery(id+"F5.wireOp",EDGE,"E25.right")])],"isStart":true}),makeQuery(id+"F6.opExtrude","CAP_FACE",FACE,{"disambiguationData":[OSD([sQuery(id+"F5.wireOp",EDGE,"E26.bottom"),sQuery(id+"F5.wireOp",EDGE,"E26.top"),sQuery(id+"F5.wireOp",EDGE,"E26.left"),sQuery(id+"F5.wireOp",EDGE,"E26.right")])],"isStart":true}),makeQuery(id+"F6.opExtrude","CAP_FACE",FACE,{"disambiguationData":[OSD([sQuery(id+"F5.wireOp",EDGE,"E27.bottom"),sQuery(id+"F5.wireOp",EDGE,"E27.top"),sQuery(id+"F5.wireOp",EDGE,"E27.left"),sQuery(id+"F5.wireOp",EDGE,"E27.right")])],"isStart":true}),makeQuery(id+"F6.opExtrude","CAP_FACE",FACE,{"disambiguationData":[OSD([sQuery(id+"F5.wireOp",EDGE,"E28.bottom"),sQuery(id+"F5.wireOp",EDGE,"E28.top"),sQuery(id+"F5.wireOp",EDGE,"E28.left"),sQuery(id+"F5.wireOp",EDGE,"E28.right")])],"isStart":true}),makeQuery(id+"F6.opExtrude","CAP_FACE",FACE,{"disambiguationData":[OSD([sQuery(id+"F5.wireOp",EDGE,"E29.bottom"),sQuery(id+"F5.wireOp",EDGE,"E29.top"),sQuery(id+"F5.wireOp",EDGE,"E29.left"),sQuery(id+"F5.wireOp",EDGE,"E29.right")])],"isStart":true}),makeQuery(id+"F6.opExtrude","CAP_FACE",FACE,{"disambiguationData":[OSD([sQuery(id+"F5.wireOp",EDGE,"E30.bottom"),sQuery(id+"F5.wireOp",EDGE,"E30.top"),sQuery(id+"F5.wireOp",EDGE,"E30.left"),sQuery(id+"F5.wireOp",EDGE,"E30.right")])],"isStart":true}),makeQuery(id+"F6.opExtrude","CAP_FACE",FACE,{"disambiguationData":[OSD([sQuery(id+"F5.wireOp",EDGE,"E31.bottom"),sQuery(id+"F5.wireOp",EDGE,"E31.top"),sQuery(id+"F5.wireOp",EDGE,"E31.left"),sQuery(id+"F5.wireOp",EDGE,"E31.right")])],"isStart":true})]});
            var sketch = newSketch(context, id + "F16", { "sketchPlane" : qUnion([Q0])});
            skLineSegment(sketch, "E67", {"start": v(-20.32, -25.82) * mm, "end": v(-20.32, -27.3) * mm});
            skLineSegment(sketch, "E68", {"start": v(-20.32, -27.3) * mm, "end": v(-25.61, -27.3) * mm});
            skLineSegment(sketch, "E69", {"start": v(-20.53, -25.82) * mm, "end": v(-20.53, -27.1) * mm});
            skLineSegment(sketch, "E70", {"start": v(-20.53, -27.1) * mm, "end": v(-25.61, -27.1) * mm});
            skLineSegment(sketch, "E71", {"start": v(-20.53, -25.82) * mm, "end": v(-20.32, -25.82) * mm});
            skLineSegment(sketch, "E72", {"start": v(-25.61, -27.1) * mm, "end": v(-25.61, -27.3) * mm});
            skSolve(sketch);
        }
        {
            var Q0;
            Q0 = qSketchRegion(id + "F16", true);
            extrude(context, id + "F17", {"entities" : qUnion([Q0]), "operationType" : NewBodyOperationType.ADD, "depth" : 19.05 * mm});
        }
        {
            var Q0;
            {var subQ0=sQuery(id+"F5.wireOp",EDGE,"E24.top");var subQ1=sQuery(id+"F2.wireOp",EDGE,"E13.right");var subQ2=sQuery(id+"F2.wireOp",EDGE,"E22");var subQ3=sQuery(id+"F5.wireOp",EDGE,"E29.right");var subQ4=sQuery(id+"F2.wireOp",EDGE,"E20");var subQ5=sQuery(id+"F5.wireOp",EDGE,"E28.right");var subQ6=sQuery(id+"F2.wireOp",EDGE,"E18");var subQ7=sQuery(id+"F5.wireOp",EDGE,"E27.top");var subQ8=sQuery(id+"F2.wireOp",EDGE,"E17");var subQ9=sQuery(id+"F5.wireOp",EDGE,"E27.bottom");var subQ10=sQuery(id+"F2.wireOp",EDGE,"E16");var subQ11=sQuery(id+"F5.wireOp",EDGE,"E26.top");var subQ12=sQuery(id+"F2.wireOp",EDGE,"E15");var subQ13=sQuery(id+"F5.wireOp",EDGE,"E26.bottom");var subQ14=sQuery(id+"F2.wireOp",EDGE,"E14");var subQ15=sQuery(id+"F2.wireOp",EDGE,"E13.left");var subQ16=sQuery(id+"F2.wireOp",EDGE,"E19");var subQ17=sQuery(id+"F5.wireOp",EDGE,"E25.top");var subQ18=sQuery(id+"F2.wireOp",EDGE,"E8");var subQ19=sQuery(id+"F5.wireOp",EDGE,"E25.bottom");var subQ20=sQuery(id+"F5.wireOp",EDGE,"E24.bottom");var subQ21=sQuery(id+"F2.wireOp",EDGE,"E13.top");var subQ22=sQuery(id+"F2.wireOp",EDGE,"E23");var subQ23=sQuery(id+"F2.wireOp",EDGE,"E11");var subQ24=sQuery(id+"F2.wireOp",EDGE,"E10");var subQ25=sQuery(id+"F2.wireOp",EDGE,"E9");var subQ26=sQuery(id+"F2.wireOp",EDGE,"E7.right");var subQ27=sQuery(id+"F2.wireOp",EDGE,"E7.left");var subQ28=sQuery(id+"F2.wireOp",EDGE,"E7.top");var subQ29=sQuery(id+"F2.wireOp",EDGE,"E7.bottom");var subQ30=sQuery(id+"F2.wireOp",EDGE,"E2.right");var subQ31=sQuery(id+"F2.wireOp",EDGE,"E2.left");var subQ32=sQuery(id+"F2.wireOp",EDGE,"E2.top");var subQ33=sQuery(id+"F2.wireOp",EDGE,"E2.bottom");var subQ34=sQuery(id+"F2.wireOp",EDGE,"E1.right");var subQ35=sQuery(id+"F2.wireOp",EDGE,"E3.bottom");var subQ36=sQuery(id+"F5.wireOp",EDGE,"E28.left");var subQ37=sQuery(id+"F2.wireOp",EDGE,"E3.right");var subQ38=sQuery(id+"F2.wireOp",EDGE,"E21");var subQ39=sQuery(id+"F5.wireOp",EDGE,"E29.left");var subQ40=sQuery(id+"F2.wireOp",EDGE,"E1.bottom");var subQ41=sQuery(id+"F2.wireOp",EDGE,"E5.left");var subQ42=sQuery(id+"F2.wireOp",EDGE,"E1.top");var subQ43=sQuery(id+"F2.wireOp",EDGE,"E6");var subQ44=sQuery(id+"F2.wireOp",EDGE,"E1.left");var subQ45=sQuery(id+"F2.wireOp",EDGE,"E3.top");var subQ46=sQuery(id+"F2.wireOp",EDGE,"E3.left");var subQ47=sQuery(id+"F2.wireOp",EDGE,"E4.bottom");var subQ48=sQuery(id+"F2.wireOp",EDGE,"E4.top");var subQ49=sQuery(id+"F2.wireOp",EDGE,"E4.left");var subQ50=sQuery(id+"F2.wireOp",EDGE,"E4.right");var subQ51=sQuery(id+"F2.wireOp",EDGE,"E5.bottom");var subQ52=sQuery(id+"F2.wireOp",EDGE,"E5.top");var subQ53=sQuery(id+"F2.wireOp",EDGE,"E5.right");var subQ54=sQuery(id+"F5.wireOp",EDGE,"E30.bottom");var subQ55=sQuery(id+"F5.wireOp",EDGE,"E30.top");var subQ56=sQuery(id+"F5.wireOp",EDGE,"E31.bottom");var subQ57=sQuery(id+"F5.wireOp",EDGE,"E31.top");Q0=makeQuery(id+"F17.boolean.opBoolean","SPLIT",FACE,{"disambiguationData":[TD([makeQuery(id+"F1.opExtrude","SWEPT_FACE",FACE,{"disambiguationData":[OSD([sQuery(id+"F0.wireOp",EDGE,"E0.left")])]})])],"derivedFrom":makeQuery(id+"F6.boolean.opBoolean","MERGE",FACE,{"derivedFrom":[makeQuery(id+"F3.boolean.opBoolean","COPY",FACE,{"derivedFrom":makeQuery(id+"F3.opExtrude","CAP_FACE",FACE,{"disambiguationData":[OSD([subQ40,subQ42,subQ44,subQ34])],"isStart":false})}),makeQuery(id+"F3.boolean.opBoolean","COPY",FACE,{"derivedFrom":makeQuery(id+"F3.opExtrude","CAP_FACE",FACE,{"disambiguationData":[OSD([subQ33,subQ32,subQ31,subQ30])],"isStart":false})}),makeQuery(id+"F3.boolean.opBoolean","COPY",FACE,{"derivedFrom":makeQuery(id+"F3.opExtrude","CAP_FACE",FACE,{"disambiguationData":[OSD([subQ35,subQ45,subQ46,subQ37])],"isStart":false})}),makeQuery(id+"F3.boolean.opBoolean","COPY",FACE,{"derivedFrom":makeQuery(id+"F3.opExtrude","CAP_FACE",FACE,{"disambiguationData":[OSD([subQ47,subQ48,subQ49,subQ50])],"isStart":false})}),makeQuery(id+"F3.boolean.opBoolean","COPY",FACE,{"derivedFrom":makeQuery(id+"F3.opExtrude","CAP_FACE",FACE,{"disambiguationData":[OSD([subQ51,subQ52,subQ41,subQ53])],"isStart":false})}),makeQuery(id+"F3.boolean.opBoolean","COPY",FACE,{"derivedFrom":makeQuery(id+"F3.opExtrude","CAP_FACE",FACE,{"disambiguationData":[OSD([subQ43,subQ29,subQ26,subQ18,subQ25,subQ24,subQ23,subQ21,subQ15,subQ1,subQ14,subQ12,subQ10,subQ16,subQ4,subQ38,subQ2,subQ22])],"isStart":false})}),makeQuery(id+"F3.boolean.opBoolean","COPY",FACE,{"derivedFrom":makeQuery(id+"F3.opExtrude","CAP_FACE",FACE,{"disambiguationData":[OSD([subQ28,subQ27,subQ8,subQ6])],"isStart":false})}),makeQuery(id+"F6.opExtrude","CAP_FACE",FACE,{"disambiguationData":[OSD([subQ20,subQ0,sQuery(id+"F5.wireOp",EDGE,"E24.left"),sQuery(id+"F5.wireOp",EDGE,"E24.right")])],"isStart":true}),makeQuery(id+"F6.opExtrude","CAP_FACE",FACE,{"disambiguationData":[OSD([subQ19,subQ17,sQuery(id+"F5.wireOp",EDGE,"E25.left"),sQuery(id+"F5.wireOp",EDGE,"E25.right")])],"isStart":true}),makeQuery(id+"F6.opExtrude","CAP_FACE",FACE,{"disambiguationData":[OSD([subQ13,subQ11,sQuery(id+"F5.wireOp",EDGE,"E26.left"),sQuery(id+"F5.wireOp",EDGE,"E26.right")])],"isStart":true}),makeQuery(id+"F6.opExtrude","CAP_FACE",FACE,{"disambiguationData":[OSD([subQ9,subQ7,sQuery(id+"F5.wireOp",EDGE,"E27.left"),sQuery(id+"F5.wireOp",EDGE,"E27.right")])],"isStart":true}),makeQuery(id+"F6.opExtrude","CAP_FACE",FACE,{"disambiguationData":[OSD([sQuery(id+"F5.wireOp",EDGE,"E28.bottom"),sQuery(id+"F5.wireOp",EDGE,"E28.top"),subQ36,subQ5])],"isStart":true}),makeQuery(id+"F6.opExtrude","CAP_FACE",FACE,{"disambiguationData":[OSD([sQuery(id+"F5.wireOp",EDGE,"E29.bottom"),sQuery(id+"F5.wireOp",EDGE,"E29.top"),subQ39,subQ3])],"isStart":true}),makeQuery(id+"F6.opExtrude","CAP_FACE",FACE,{"disambiguationData":[OSD([subQ54,subQ55,sQuery(id+"F5.wireOp",EDGE,"E30.left"),sQuery(id+"F5.wireOp",EDGE,"E30.right")])],"isStart":true}),makeQuery(id+"F6.opExtrude","CAP_FACE",FACE,{"disambiguationData":[OSD([subQ56,subQ57,sQuery(id+"F5.wireOp",EDGE,"E31.left"),sQuery(id+"F5.wireOp",EDGE,"E31.right")])],"isStart":true})]})});}
            var sketch = newSketch(context, id + "F18", { "sketchPlane" : qUnion([Q0])});
            skLineSegment(sketch, "E73.bottom", {"start": v(-24.98, -26.33) * mm, "end": v(-21.17, -26.33) * mm});
            skLineSegment(sketch, "E73.top", {"start": v(-24.98, -28.05) * mm, "end": v(-21.17, -28.05) * mm});
            skLineSegment(sketch, "E73.left", {"start": v(-24.98, -26.33) * mm, "end": v(-24.98, -28.05) * mm});
            skLineSegment(sketch, "E73.right", {"start": v(-21.17, -26.33) * mm, "end": v(-21.17, -28.05) * mm});
            skSolve(sketch);
        }
        {
            var Q0;
            Q0 = qSketchRegion(id + "F18", true);
            extrude(context, id + "F19", {"entities" : qUnion([Q0]), "operationType" : NewBodyOperationType.REMOVE, "depth" : 25.4 * mm});
        }
        {
            var Q0;
            {var subQ0=sQuery(id+"F2.wireOp",EDGE,"E4.bottom");var subQ2=sQuery(id+"F2.wireOp",EDGE,"E4.left");var subQ4=sQuery(id+"F5.wireOp",EDGE,"E31.top");var subQ5=sQuery(id+"F5.wireOp",EDGE,"E31.bottom");var subQ6=sQuery(id+"F5.wireOp",EDGE,"E30.top");var subQ7=sQuery(id+"F5.wireOp",EDGE,"E30.bottom");var subQ8=sQuery(id+"F5.wireOp",EDGE,"E29.right");var subQ9=sQuery(id+"F5.wireOp",EDGE,"E29.left");var subQ10=sQuery(id+"F5.wireOp",EDGE,"E28.right");var subQ11=sQuery(id+"F5.wireOp",EDGE,"E28.left");var subQ12=sQuery(id+"F5.wireOp",EDGE,"E27.top");var subQ13=sQuery(id+"F5.wireOp",EDGE,"E27.bottom");var subQ14=sQuery(id+"F5.wireOp",EDGE,"E26.top");var subQ15=sQuery(id+"F5.wireOp",EDGE,"E26.bottom");var subQ16=sQuery(id+"F5.wireOp",EDGE,"E25.top");var subQ17=sQuery(id+"F5.wireOp",EDGE,"E25.bottom");var subQ18=sQuery(id+"F5.wireOp",EDGE,"E24.top");var subQ19=sQuery(id+"F5.wireOp",EDGE,"E24.bottom");var subQ20=sQuery(id+"F2.wireOp",EDGE,"E18");var subQ21=sQuery(id+"F2.wireOp",EDGE,"E17");var subQ22=sQuery(id+"F2.wireOp",EDGE,"E7.left");var subQ23=sQuery(id+"F2.wireOp",EDGE,"E7.top");var subQ24=sQuery(id+"F2.wireOp",EDGE,"E23");var subQ25=sQuery(id+"F2.wireOp",EDGE,"E22");var subQ26=sQuery(id+"F2.wireOp",EDGE,"E21");var subQ27=sQuery(id+"F2.wireOp",EDGE,"E20");var subQ28=sQuery(id+"F2.wireOp",EDGE,"E19");var subQ29=sQuery(id+"F2.wireOp",EDGE,"E16");var subQ30=sQuery(id+"F2.wireOp",EDGE,"E15");var subQ31=sQuery(id+"F2.wireOp",EDGE,"E14");var subQ32=sQuery(id+"F2.wireOp",EDGE,"E13.right");var subQ33=sQuery(id+"F2.wireOp",EDGE,"E13.left");var subQ34=sQuery(id+"F2.wireOp",EDGE,"E13.top");var subQ35=sQuery(id+"F2.wireOp",EDGE,"E11");var subQ36=sQuery(id+"F2.wireOp",EDGE,"E10");var subQ37=sQuery(id+"F2.wireOp",EDGE,"E9");var subQ38=sQuery(id+"F2.wireOp",EDGE,"E8");var subQ39=sQuery(id+"F2.wireOp",EDGE,"E7.right");var subQ40=sQuery(id+"F2.wireOp",EDGE,"E7.bottom");var subQ41=sQuery(id+"F2.wireOp",EDGE,"E6");var subQ42=sQuery(id+"F2.wireOp",EDGE,"E5.right");var subQ43=sQuery(id+"F2.wireOp",EDGE,"E5.left");var subQ44=sQuery(id+"F2.wireOp",EDGE,"E5.top");var subQ45=sQuery(id+"F2.wireOp",EDGE,"E5.bottom");var subQ46=sQuery(id+"F2.wireOp",EDGE,"E4.right");var subQ47=sQuery(id+"F2.wireOp",EDGE,"E4.top");var subQ48=sQuery(id+"F2.wireOp",EDGE,"E3.right");var subQ49=sQuery(id+"F2.wireOp",EDGE,"E3.left");var subQ50=sQuery(id+"F2.wireOp",EDGE,"E3.top");var subQ51=sQuery(id+"F2.wireOp",EDGE,"E3.bottom");var subQ52=sQuery(id+"F2.wireOp",EDGE,"E2.right");var subQ53=sQuery(id+"F2.wireOp",EDGE,"E2.left");var subQ54=sQuery(id+"F2.wireOp",EDGE,"E2.top");var subQ55=sQuery(id+"F2.wireOp",EDGE,"E2.bottom");var subQ56=sQuery(id+"F2.wireOp",EDGE,"E1.right");var subQ57=sQuery(id+"F2.wireOp",EDGE,"E1.left");var subQ58=sQuery(id+"F2.wireOp",EDGE,"E1.top");var subQ59=sQuery(id+"F2.wireOp",EDGE,"E1.bottom");var subQ60=makeQuery(id+"F6.boolean.opBoolean","MERGE",FACE,{"derivedFrom":[makeQuery(id+"F3.boolean.opBoolean","COPY",FACE,{"derivedFrom":makeQuery(id+"F3.opExtrude","CAP_FACE",FACE,{"disambiguationData":[OSD([subQ59,subQ58,subQ57,subQ56])],"isStart":false})}),makeQuery(id+"F3.boolean.opBoolean","COPY",FACE,{"derivedFrom":makeQuery(id+"F3.opExtrude","CAP_FACE",FACE,{"disambiguationData":[OSD([subQ55,subQ54,subQ53,subQ52])],"isStart":false})}),makeQuery(id+"F3.boolean.opBoolean","COPY",FACE,{"derivedFrom":makeQuery(id+"F3.opExtrude","CAP_FACE",FACE,{"disambiguationData":[OSD([subQ51,subQ50,subQ49,subQ48])],"isStart":false})}),makeQuery(id+"F3.boolean.opBoolean","COPY",FACE,{"derivedFrom":makeQuery(id+"F3.opExtrude","CAP_FACE",FACE,{"disambiguationData":[OSD([subQ0,subQ47,subQ2,subQ46])],"isStart":false})}),makeQuery(id+"F3.boolean.opBoolean","COPY",FACE,{"derivedFrom":makeQuery(id+"F3.opExtrude","CAP_FACE",FACE,{"disambiguationData":[OSD([subQ45,subQ44,subQ43,subQ42])],"isStart":false})}),makeQuery(id+"F3.boolean.opBoolean","COPY",FACE,{"derivedFrom":makeQuery(id+"F3.opExtrude","CAP_FACE",FACE,{"disambiguationData":[OSD([subQ41,subQ40,subQ39,subQ38,subQ37,subQ36,subQ35,subQ34,subQ33,subQ32,subQ31,subQ30,subQ29,subQ28,subQ27,subQ26,subQ25,subQ24])],"isStart":false})}),makeQuery(id+"F3.boolean.opBoolean","COPY",FACE,{"derivedFrom":makeQuery(id+"F3.opExtrude","CAP_FACE",FACE,{"disambiguationData":[OSD([subQ23,subQ22,subQ21,subQ20])],"isStart":false})}),makeQuery(id+"F6.opExtrude","CAP_FACE",FACE,{"disambiguationData":[OSD([subQ19,subQ18,sQuery(id+"F5.wireOp",EDGE,"E24.left"),sQuery(id+"F5.wireOp",EDGE,"E24.right")])],"isStart":true}),makeQuery(id+"F6.opExtrude","CAP_FACE",FACE,{"disambiguationData":[OSD([subQ17,subQ16,sQuery(id+"F5.wireOp",EDGE,"E25.left"),sQuery(id+"F5.wireOp",EDGE,"E25.right")])],"isStart":true}),makeQuery(id+"F6.opExtrude","CAP_FACE",FACE,{"disambiguationData":[OSD([subQ15,subQ14,sQuery(id+"F5.wireOp",EDGE,"E26.left"),sQuery(id+"F5.wireOp",EDGE,"E26.right")])],"isStart":true}),makeQuery(id+"F6.opExtrude","CAP_FACE",FACE,{"disambiguationData":[OSD([subQ13,subQ12,sQuery(id+"F5.wireOp",EDGE,"E27.left"),sQuery(id+"F5.wireOp",EDGE,"E27.right")])],"isStart":true}),makeQuery(id+"F6.opExtrude","CAP_FACE",FACE,{"disambiguationData":[OSD([sQuery(id+"F5.wireOp",EDGE,"E28.bottom"),sQuery(id+"F5.wireOp",EDGE,"E28.top"),subQ11,subQ10])],"isStart":true}),makeQuery(id+"F6.opExtrude","CAP_FACE",FACE,{"disambiguationData":[OSD([sQuery(id+"F5.wireOp",EDGE,"E29.bottom"),sQuery(id+"F5.wireOp",EDGE,"E29.top"),subQ9,subQ8])],"isStart":true}),makeQuery(id+"F6.opExtrude","CAP_FACE",FACE,{"disambiguationData":[OSD([subQ7,subQ6,sQuery(id+"F5.wireOp",EDGE,"E30.left"),sQuery(id+"F5.wireOp",EDGE,"E30.right")])],"isStart":true}),makeQuery(id+"F6.opExtrude","CAP_FACE",FACE,{"disambiguationData":[OSD([subQ5,subQ4,sQuery(id+"F5.wireOp",EDGE,"E31.left"),sQuery(id+"F5.wireOp",EDGE,"E31.right")])],"isStart":true})]});Q0=makeQuery(id+"F19.boolean.opBoolean","MERGE",FACE,{"derivedFrom":[makeQuery(id+"F17.boolean.opBoolean","SPLIT",FACE,{"disambiguationData":[TD([makeQuery(id+"F1.opExtrude","SWEPT_FACE",FACE,{"disambiguationData":[OSD([sQuery(id+"F0.wireOp",EDGE,"E0.left")])]})])],"derivedFrom":subQ60}),makeQuery(id+"F17.boolean.opBoolean","SPLIT",FACE,{"disambiguationData":[TD([makeQuery(id+"F17.opExtrude","SWEPT_FACE",FACE,{"disambiguationData":[OSD([sQuery(id+"F16.wireOp",EDGE,"E69")])]})])],"derivedFrom":subQ60}),makeQuery(id+"F19.opExtrude","CAP_FACE",FACE,{"disambiguationData":[OSD([sQuery(id+"F18.wireOp",EDGE,"E73.bottom"),sQuery(id+"F18.wireOp",EDGE,"E73.top"),sQuery(id+"F18.wireOp",EDGE,"E73.left"),sQuery(id+"F18.wireOp",EDGE,"E73.right")])],"isStart":true})]});}
            var sketch = newSketch(context, id + "F20", { "sketchPlane" : qUnion([Q0])});
            skArc(sketch, "E74", {"start": v(-23.07, -27.3) * mm, "mid": v(-22.51, -28.65) * mm, "end": v(-21.17, -29.2) * mm});
            skArc(sketch, "E75", {"start": v(-23.07, -27.3) * mm, "mid": v(-23.63, -28.65) * mm, "end": v(-24.98, -29.2) * mm});
            skArc(sketch, "E76", {"start": v(-23.2, -27.3) * mm, "mid": v(-23.72, -28.56) * mm, "end": v(-24.98, -29.08) * mm});
            skArc(sketch, "E77", {"start": v(-22.94, -27.3) * mm, "mid": v(-22.42, -28.56) * mm, "end": v(-21.17, -29.08) * mm});
            skLineSegment(sketch, "E78", {"start": v(-23.2, -27.3) * mm, "end": v(-23.07, -27.3) * mm});
            skLineSegment(sketch, "E79", {"start": v(-23.07, -27.3) * mm, "end": v(-22.94, -27.3) * mm});
            skLineSegment(sketch, "E80", {"start": v(-21.17, -29.2) * mm, "end": v(-21.17, -29.08) * mm});
            skLineSegment(sketch, "E81", {"start": v(-24.98, -29.2) * mm, "end": v(-24.98, -29.08) * mm});
            skSolve(sketch);
        }
        {
            var Q0;
            Q0 = qSketchRegion(id + "F20", true);
            extrude(context, id + "F21", {"entities" : qUnion([Q0]), "operationType" : NewBodyOperationType.REMOVE, "oppositeDirection" : true, "depth" : 0.25 * mm});
        }
        {
            var Q0;
            {var subQ0=sQuery(id+"F2.wireOp",EDGE,"E4.bottom");var subQ2=sQuery(id+"F2.wireOp",EDGE,"E4.left");var subQ4=sQuery(id+"F5.wireOp",EDGE,"E31.top");var subQ5=sQuery(id+"F5.wireOp",EDGE,"E31.bottom");var subQ6=sQuery(id+"F5.wireOp",EDGE,"E30.top");var subQ7=sQuery(id+"F5.wireOp",EDGE,"E30.bottom");var subQ8=sQuery(id+"F5.wireOp",EDGE,"E29.right");var subQ9=sQuery(id+"F5.wireOp",EDGE,"E29.left");var subQ10=sQuery(id+"F5.wireOp",EDGE,"E28.right");var subQ11=sQuery(id+"F5.wireOp",EDGE,"E28.left");var subQ12=sQuery(id+"F5.wireOp",EDGE,"E27.top");var subQ13=sQuery(id+"F5.wireOp",EDGE,"E27.bottom");var subQ14=sQuery(id+"F5.wireOp",EDGE,"E26.top");var subQ15=sQuery(id+"F5.wireOp",EDGE,"E26.bottom");var subQ16=sQuery(id+"F5.wireOp",EDGE,"E25.top");var subQ17=sQuery(id+"F5.wireOp",EDGE,"E25.bottom");var subQ18=sQuery(id+"F5.wireOp",EDGE,"E24.top");var subQ19=sQuery(id+"F5.wireOp",EDGE,"E24.bottom");var subQ20=sQuery(id+"F2.wireOp",EDGE,"E18");var subQ21=sQuery(id+"F2.wireOp",EDGE,"E17");var subQ22=sQuery(id+"F2.wireOp",EDGE,"E7.left");var subQ23=sQuery(id+"F2.wireOp",EDGE,"E7.top");var subQ24=sQuery(id+"F2.wireOp",EDGE,"E23");var subQ25=sQuery(id+"F2.wireOp",EDGE,"E22");var subQ26=sQuery(id+"F2.wireOp",EDGE,"E21");var subQ27=sQuery(id+"F2.wireOp",EDGE,"E20");var subQ28=sQuery(id+"F2.wireOp",EDGE,"E19");var subQ29=sQuery(id+"F2.wireOp",EDGE,"E16");var subQ30=sQuery(id+"F2.wireOp",EDGE,"E15");var subQ31=sQuery(id+"F2.wireOp",EDGE,"E14");var subQ32=sQuery(id+"F2.wireOp",EDGE,"E13.right");var subQ33=sQuery(id+"F2.wireOp",EDGE,"E13.left");var subQ34=sQuery(id+"F2.wireOp",EDGE,"E13.top");var subQ35=sQuery(id+"F2.wireOp",EDGE,"E11");var subQ36=sQuery(id+"F2.wireOp",EDGE,"E10");var subQ37=sQuery(id+"F2.wireOp",EDGE,"E9");var subQ38=sQuery(id+"F2.wireOp",EDGE,"E8");var subQ39=sQuery(id+"F2.wireOp",EDGE,"E7.right");var subQ40=sQuery(id+"F2.wireOp",EDGE,"E7.bottom");var subQ41=sQuery(id+"F2.wireOp",EDGE,"E6");var subQ42=sQuery(id+"F2.wireOp",EDGE,"E5.right");var subQ43=sQuery(id+"F2.wireOp",EDGE,"E5.left");var subQ44=sQuery(id+"F2.wireOp",EDGE,"E5.top");var subQ45=sQuery(id+"F2.wireOp",EDGE,"E5.bottom");var subQ46=sQuery(id+"F2.wireOp",EDGE,"E4.right");var subQ47=sQuery(id+"F2.wireOp",EDGE,"E4.top");var subQ48=sQuery(id+"F2.wireOp",EDGE,"E3.right");var subQ49=sQuery(id+"F2.wireOp",EDGE,"E3.left");var subQ50=sQuery(id+"F2.wireOp",EDGE,"E3.top");var subQ51=sQuery(id+"F2.wireOp",EDGE,"E3.bottom");var subQ52=sQuery(id+"F2.wireOp",EDGE,"E2.right");var subQ53=sQuery(id+"F2.wireOp",EDGE,"E2.left");var subQ54=sQuery(id+"F2.wireOp",EDGE,"E2.top");var subQ55=sQuery(id+"F2.wireOp",EDGE,"E2.bottom");var subQ56=sQuery(id+"F2.wireOp",EDGE,"E1.right");var subQ57=sQuery(id+"F2.wireOp",EDGE,"E1.left");var subQ58=sQuery(id+"F2.wireOp",EDGE,"E1.top");var subQ59=sQuery(id+"F2.wireOp",EDGE,"E1.bottom");var subQ60=makeQuery(id+"F6.boolean.opBoolean","MERGE",FACE,{"derivedFrom":[makeQuery(id+"F3.boolean.opBoolean","COPY",FACE,{"derivedFrom":makeQuery(id+"F3.opExtrude","CAP_FACE",FACE,{"disambiguationData":[OSD([subQ59,subQ58,subQ57,subQ56])],"isStart":false})}),makeQuery(id+"F3.boolean.opBoolean","COPY",FACE,{"derivedFrom":makeQuery(id+"F3.opExtrude","CAP_FACE",FACE,{"disambiguationData":[OSD([subQ55,subQ54,subQ53,subQ52])],"isStart":false})}),makeQuery(id+"F3.boolean.opBoolean","COPY",FACE,{"derivedFrom":makeQuery(id+"F3.opExtrude","CAP_FACE",FACE,{"disambiguationData":[OSD([subQ51,subQ50,subQ49,subQ48])],"isStart":false})}),makeQuery(id+"F3.boolean.opBoolean","COPY",FACE,{"derivedFrom":makeQuery(id+"F3.opExtrude","CAP_FACE",FACE,{"disambiguationData":[OSD([subQ0,subQ47,subQ2,subQ46])],"isStart":false})}),makeQuery(id+"F3.boolean.opBoolean","COPY",FACE,{"derivedFrom":makeQuery(id+"F3.opExtrude","CAP_FACE",FACE,{"disambiguationData":[OSD([subQ45,subQ44,subQ43,subQ42])],"isStart":false})}),makeQuery(id+"F3.boolean.opBoolean","COPY",FACE,{"derivedFrom":makeQuery(id+"F3.opExtrude","CAP_FACE",FACE,{"disambiguationData":[OSD([subQ41,subQ40,subQ39,subQ38,subQ37,subQ36,subQ35,subQ34,subQ33,subQ32,subQ31,subQ30,subQ29,subQ28,subQ27,subQ26,subQ25,subQ24])],"isStart":false})}),makeQuery(id+"F3.boolean.opBoolean","COPY",FACE,{"derivedFrom":makeQuery(id+"F3.opExtrude","CAP_FACE",FACE,{"disambiguationData":[OSD([subQ23,subQ22,subQ21,subQ20])],"isStart":false})}),makeQuery(id+"F6.opExtrude","CAP_FACE",FACE,{"disambiguationData":[OSD([subQ19,subQ18,sQuery(id+"F5.wireOp",EDGE,"E24.left"),sQuery(id+"F5.wireOp",EDGE,"E24.right")])],"isStart":true}),makeQuery(id+"F6.opExtrude","CAP_FACE",FACE,{"disambiguationData":[OSD([subQ17,subQ16,sQuery(id+"F5.wireOp",EDGE,"E25.left"),sQuery(id+"F5.wireOp",EDGE,"E25.right")])],"isStart":true}),makeQuery(id+"F6.opExtrude","CAP_FACE",FACE,{"disambiguationData":[OSD([subQ15,subQ14,sQuery(id+"F5.wireOp",EDGE,"E26.left"),sQuery(id+"F5.wireOp",EDGE,"E26.right")])],"isStart":true}),makeQuery(id+"F6.opExtrude","CAP_FACE",FACE,{"disambiguationData":[OSD([subQ13,subQ12,sQuery(id+"F5.wireOp",EDGE,"E27.left"),sQuery(id+"F5.wireOp",EDGE,"E27.right")])],"isStart":true}),makeQuery(id+"F6.opExtrude","CAP_FACE",FACE,{"disambiguationData":[OSD([sQuery(id+"F5.wireOp",EDGE,"E28.bottom"),sQuery(id+"F5.wireOp",EDGE,"E28.top"),subQ11,subQ10])],"isStart":true}),makeQuery(id+"F6.opExtrude","CAP_FACE",FACE,{"disambiguationData":[OSD([sQuery(id+"F5.wireOp",EDGE,"E29.bottom"),sQuery(id+"F5.wireOp",EDGE,"E29.top"),subQ9,subQ8])],"isStart":true}),makeQuery(id+"F6.opExtrude","CAP_FACE",FACE,{"disambiguationData":[OSD([subQ7,subQ6,sQuery(id+"F5.wireOp",EDGE,"E30.left"),sQuery(id+"F5.wireOp",EDGE,"E30.right")])],"isStart":true}),makeQuery(id+"F6.opExtrude","CAP_FACE",FACE,{"disambiguationData":[OSD([subQ5,subQ4,sQuery(id+"F5.wireOp",EDGE,"E31.left"),sQuery(id+"F5.wireOp",EDGE,"E31.right")])],"isStart":true})]});Q0=makeQuery(id+"F19.boolean.opBoolean","MERGE",FACE,{"derivedFrom":[makeQuery(id+"F17.boolean.opBoolean","SPLIT",FACE,{"disambiguationData":[TD([makeQuery(id+"F1.opExtrude","SWEPT_FACE",FACE,{"disambiguationData":[OSD([sQuery(id+"F0.wireOp",EDGE,"E0.left")])]})])],"derivedFrom":subQ60}),makeQuery(id+"F17.boolean.opBoolean","SPLIT",FACE,{"disambiguationData":[TD([makeQuery(id+"F17.opExtrude","SWEPT_FACE",FACE,{"disambiguationData":[OSD([sQuery(id+"F16.wireOp",EDGE,"E69")])]})])],"derivedFrom":subQ60}),makeQuery(id+"F19.opExtrude","CAP_FACE",FACE,{"disambiguationData":[OSD([sQuery(id+"F18.wireOp",EDGE,"E73.bottom"),sQuery(id+"F18.wireOp",EDGE,"E73.top"),sQuery(id+"F18.wireOp",EDGE,"E73.left"),sQuery(id+"F18.wireOp",EDGE,"E73.right")])],"isStart":true})]});}
            var sketch = newSketch(context, id + "F22", { "sketchPlane" : qUnion([Q0])});
            skArc(sketch, "E82", {"start": v(51.43, -31.33) * mm, "mid": v(46.94, -33.19) * mm, "end": v(45.08, -37.68) * mm});
            skArc(sketch, "E83", {"start": v(51.43, -31.45) * mm, "mid": v(47.03, -33.28) * mm, "end": v(45.21, -37.68) * mm});
            skArc(sketch, "E84", {"start": v(51.43, 31.33) * mm, "mid": v(46.94, 33.19) * mm, "end": v(45.08, 37.68) * mm});
            skArc(sketch, "E85", {"start": v(51.43, 31.45) * mm, "mid": v(47.03, 33.28) * mm, "end": v(45.21, 37.68) * mm});
            skLineSegment(sketch, "E86", {"start": v(45.08, 37.68) * mm, "end": v(45.21, 37.68) * mm});
            skLineSegment(sketch, "E87", {"start": v(51.43, 31.45) * mm, "end": v(51.43, 31.33) * mm});
            skLineSegment(sketch, "E88", {"start": v(51.43, -31.33) * mm, "end": v(51.43, -31.45) * mm});
            skLineSegment(sketch, "E89", {"start": v(45.08, -37.68) * mm, "end": v(45.21, -37.68) * mm});
            skSolve(sketch);
        }
        {
            var Q0;
            Q0 = qSketchRegion(id + "F22", true);
            extrude(context, id + "F23", {"entities" : qUnion([Q0]), "operationType" : NewBodyOperationType.REMOVE, "oppositeDirection" : true, "depth" : 0.25 * mm});
        }
        {
            var Q0;
            {var subQ0=sQuery(id+"F2.wireOp",EDGE,"E4.bottom");var subQ2=sQuery(id+"F2.wireOp",EDGE,"E4.left");var subQ4=sQuery(id+"F5.wireOp",EDGE,"E31.top");var subQ5=sQuery(id+"F5.wireOp",EDGE,"E31.bottom");var subQ6=sQuery(id+"F5.wireOp",EDGE,"E30.top");var subQ7=sQuery(id+"F5.wireOp",EDGE,"E30.bottom");var subQ8=sQuery(id+"F5.wireOp",EDGE,"E29.right");var subQ9=sQuery(id+"F5.wireOp",EDGE,"E29.left");var subQ10=sQuery(id+"F5.wireOp",EDGE,"E28.right");var subQ11=sQuery(id+"F5.wireOp",EDGE,"E28.left");var subQ12=sQuery(id+"F5.wireOp",EDGE,"E27.top");var subQ13=sQuery(id+"F5.wireOp",EDGE,"E27.bottom");var subQ14=sQuery(id+"F5.wireOp",EDGE,"E26.top");var subQ15=sQuery(id+"F5.wireOp",EDGE,"E26.bottom");var subQ16=sQuery(id+"F5.wireOp",EDGE,"E25.top");var subQ17=sQuery(id+"F5.wireOp",EDGE,"E25.bottom");var subQ18=sQuery(id+"F5.wireOp",EDGE,"E24.top");var subQ19=sQuery(id+"F5.wireOp",EDGE,"E24.bottom");var subQ20=sQuery(id+"F2.wireOp",EDGE,"E18");var subQ21=sQuery(id+"F2.wireOp",EDGE,"E17");var subQ22=sQuery(id+"F2.wireOp",EDGE,"E7.left");var subQ23=sQuery(id+"F2.wireOp",EDGE,"E7.top");var subQ24=sQuery(id+"F2.wireOp",EDGE,"E23");var subQ25=sQuery(id+"F2.wireOp",EDGE,"E22");var subQ26=sQuery(id+"F2.wireOp",EDGE,"E21");var subQ27=sQuery(id+"F2.wireOp",EDGE,"E20");var subQ28=sQuery(id+"F2.wireOp",EDGE,"E19");var subQ29=sQuery(id+"F2.wireOp",EDGE,"E16");var subQ30=sQuery(id+"F2.wireOp",EDGE,"E15");var subQ31=sQuery(id+"F2.wireOp",EDGE,"E14");var subQ32=sQuery(id+"F2.wireOp",EDGE,"E13.right");var subQ33=sQuery(id+"F2.wireOp",EDGE,"E13.left");var subQ34=sQuery(id+"F2.wireOp",EDGE,"E13.top");var subQ35=sQuery(id+"F2.wireOp",EDGE,"E11");var subQ36=sQuery(id+"F2.wireOp",EDGE,"E10");var subQ37=sQuery(id+"F2.wireOp",EDGE,"E9");var subQ38=sQuery(id+"F2.wireOp",EDGE,"E8");var subQ39=sQuery(id+"F2.wireOp",EDGE,"E7.right");var subQ40=sQuery(id+"F2.wireOp",EDGE,"E7.bottom");var subQ41=sQuery(id+"F2.wireOp",EDGE,"E6");var subQ42=sQuery(id+"F2.wireOp",EDGE,"E5.right");var subQ43=sQuery(id+"F2.wireOp",EDGE,"E5.left");var subQ44=sQuery(id+"F2.wireOp",EDGE,"E5.top");var subQ45=sQuery(id+"F2.wireOp",EDGE,"E5.bottom");var subQ46=sQuery(id+"F2.wireOp",EDGE,"E4.right");var subQ47=sQuery(id+"F2.wireOp",EDGE,"E4.top");var subQ48=sQuery(id+"F2.wireOp",EDGE,"E3.right");var subQ49=sQuery(id+"F2.wireOp",EDGE,"E3.left");var subQ50=sQuery(id+"F2.wireOp",EDGE,"E3.top");var subQ51=sQuery(id+"F2.wireOp",EDGE,"E3.bottom");var subQ52=sQuery(id+"F2.wireOp",EDGE,"E2.right");var subQ53=sQuery(id+"F2.wireOp",EDGE,"E2.left");var subQ54=sQuery(id+"F2.wireOp",EDGE,"E2.top");var subQ55=sQuery(id+"F2.wireOp",EDGE,"E2.bottom");var subQ56=sQuery(id+"F2.wireOp",EDGE,"E1.right");var subQ57=sQuery(id+"F2.wireOp",EDGE,"E1.left");var subQ58=sQuery(id+"F2.wireOp",EDGE,"E1.top");var subQ59=sQuery(id+"F2.wireOp",EDGE,"E1.bottom");var subQ60=makeQuery(id+"F6.boolean.opBoolean","MERGE",FACE,{"derivedFrom":[makeQuery(id+"F3.boolean.opBoolean","COPY",FACE,{"derivedFrom":makeQuery(id+"F3.opExtrude","CAP_FACE",FACE,{"disambiguationData":[OSD([subQ59,subQ58,subQ57,subQ56])],"isStart":false})}),makeQuery(id+"F3.boolean.opBoolean","COPY",FACE,{"derivedFrom":makeQuery(id+"F3.opExtrude","CAP_FACE",FACE,{"disambiguationData":[OSD([subQ55,subQ54,subQ53,subQ52])],"isStart":false})}),makeQuery(id+"F3.boolean.opBoolean","COPY",FACE,{"derivedFrom":makeQuery(id+"F3.opExtrude","CAP_FACE",FACE,{"disambiguationData":[OSD([subQ51,subQ50,subQ49,subQ48])],"isStart":false})}),makeQuery(id+"F3.boolean.opBoolean","COPY",FACE,{"derivedFrom":makeQuery(id+"F3.opExtrude","CAP_FACE",FACE,{"disambiguationData":[OSD([subQ0,subQ47,subQ2,subQ46])],"isStart":false})}),makeQuery(id+"F3.boolean.opBoolean","COPY",FACE,{"derivedFrom":makeQuery(id+"F3.opExtrude","CAP_FACE",FACE,{"disambiguationData":[OSD([subQ45,subQ44,subQ43,subQ42])],"isStart":false})}),makeQuery(id+"F3.boolean.opBoolean","COPY",FACE,{"derivedFrom":makeQuery(id+"F3.opExtrude","CAP_FACE",FACE,{"disambiguationData":[OSD([subQ41,subQ40,subQ39,subQ38,subQ37,subQ36,subQ35,subQ34,subQ33,subQ32,subQ31,subQ30,subQ29,subQ28,subQ27,subQ26,subQ25,subQ24])],"isStart":false})}),makeQuery(id+"F3.boolean.opBoolean","COPY",FACE,{"derivedFrom":makeQuery(id+"F3.opExtrude","CAP_FACE",FACE,{"disambiguationData":[OSD([subQ23,subQ22,subQ21,subQ20])],"isStart":false})}),makeQuery(id+"F6.opExtrude","CAP_FACE",FACE,{"disambiguationData":[OSD([subQ19,subQ18,sQuery(id+"F5.wireOp",EDGE,"E24.left"),sQuery(id+"F5.wireOp",EDGE,"E24.right")])],"isStart":true}),makeQuery(id+"F6.opExtrude","CAP_FACE",FACE,{"disambiguationData":[OSD([subQ17,subQ16,sQuery(id+"F5.wireOp",EDGE,"E25.left"),sQuery(id+"F5.wireOp",EDGE,"E25.right")])],"isStart":true}),makeQuery(id+"F6.opExtrude","CAP_FACE",FACE,{"disambiguationData":[OSD([subQ15,subQ14,sQuery(id+"F5.wireOp",EDGE,"E26.left"),sQuery(id+"F5.wireOp",EDGE,"E26.right")])],"isStart":true}),makeQuery(id+"F6.opExtrude","CAP_FACE",FACE,{"disambiguationData":[OSD([subQ13,subQ12,sQuery(id+"F5.wireOp",EDGE,"E27.left"),sQuery(id+"F5.wireOp",EDGE,"E27.right")])],"isStart":true}),makeQuery(id+"F6.opExtrude","CAP_FACE",FACE,{"disambiguationData":[OSD([sQuery(id+"F5.wireOp",EDGE,"E28.bottom"),sQuery(id+"F5.wireOp",EDGE,"E28.top"),subQ11,subQ10])],"isStart":true}),makeQuery(id+"F6.opExtrude","CAP_FACE",FACE,{"disambiguationData":[OSD([sQuery(id+"F5.wireOp",EDGE,"E29.bottom"),sQuery(id+"F5.wireOp",EDGE,"E29.top"),subQ9,subQ8])],"isStart":true}),makeQuery(id+"F6.opExtrude","CAP_FACE",FACE,{"disambiguationData":[OSD([subQ7,subQ6,sQuery(id+"F5.wireOp",EDGE,"E30.left"),sQuery(id+"F5.wireOp",EDGE,"E30.right")])],"isStart":true}),makeQuery(id+"F6.opExtrude","CAP_FACE",FACE,{"disambiguationData":[OSD([subQ5,subQ4,sQuery(id+"F5.wireOp",EDGE,"E31.left"),sQuery(id+"F5.wireOp",EDGE,"E31.right")])],"isStart":true})]});Q0=makeQuery(id+"F19.boolean.opBoolean","MERGE",FACE,{"derivedFrom":[makeQuery(id+"F17.boolean.opBoolean","SPLIT",FACE,{"disambiguationData":[TD([makeQuery(id+"F1.opExtrude","SWEPT_FACE",FACE,{"disambiguationData":[OSD([sQuery(id+"F0.wireOp",EDGE,"E0.left")])]})])],"derivedFrom":subQ60}),makeQuery(id+"F17.boolean.opBoolean","SPLIT",FACE,{"disambiguationData":[TD([makeQuery(id+"F17.opExtrude","SWEPT_FACE",FACE,{"disambiguationData":[OSD([sQuery(id+"F16.wireOp",EDGE,"E69")])]})])],"derivedFrom":subQ60}),makeQuery(id+"F19.opExtrude","CAP_FACE",FACE,{"disambiguationData":[OSD([sQuery(id+"F18.wireOp",EDGE,"E73.bottom"),sQuery(id+"F18.wireOp",EDGE,"E73.top"),sQuery(id+"F18.wireOp",EDGE,"E73.left"),sQuery(id+"F18.wireOp",EDGE,"E73.right")])],"isStart":true})]});}
            var sketch = newSketch(context, id + "F24", { "sketchPlane" : qUnion([Q0])});
            skLineSegment(sketch, "E90.bottom", {"start": v(-11.64, 40.88) * mm, "end": v(-5.3, 40.88) * mm});
            skLineSegment(sketch, "E90.top", {"start": v(-11.64, 34.49) * mm, "end": v(-5.3, 34.49) * mm});
            skLineSegment(sketch, "E90.left", {"start": v(-11.64, 40.88) * mm, "end": v(-11.64, 34.49) * mm});
            skLineSegment(sketch, "E90.right", {"start": v(-5.3, 40.88) * mm, "end": v(-5.3, 34.49) * mm});
            skSolve(sketch);
        }
        {
            var Q0;
            Q0 = qSketchRegion(id + "F24", true);
            extrude(context, id + "F25", {"entities" : qUnion([Q0]), "operationType" : NewBodyOperationType.REMOVE, "depth" : 25.4 * mm});
        }
        {
            var Q0;
            {var subQ0=sQuery(id+"F2.wireOp",EDGE,"E4.bottom");var subQ2=sQuery(id+"F2.wireOp",EDGE,"E4.left");var subQ4=sQuery(id+"F5.wireOp",EDGE,"E31.top");var subQ5=sQuery(id+"F5.wireOp",EDGE,"E31.bottom");var subQ6=sQuery(id+"F5.wireOp",EDGE,"E30.top");var subQ7=sQuery(id+"F5.wireOp",EDGE,"E30.bottom");var subQ8=sQuery(id+"F5.wireOp",EDGE,"E29.right");var subQ9=sQuery(id+"F5.wireOp",EDGE,"E29.left");var subQ10=sQuery(id+"F5.wireOp",EDGE,"E28.right");var subQ11=sQuery(id+"F5.wireOp",EDGE,"E28.left");var subQ12=sQuery(id+"F5.wireOp",EDGE,"E27.top");var subQ13=sQuery(id+"F5.wireOp",EDGE,"E27.bottom");var subQ14=sQuery(id+"F5.wireOp",EDGE,"E26.top");var subQ15=sQuery(id+"F5.wireOp",EDGE,"E26.bottom");var subQ16=sQuery(id+"F5.wireOp",EDGE,"E25.top");var subQ17=sQuery(id+"F5.wireOp",EDGE,"E25.bottom");var subQ18=sQuery(id+"F5.wireOp",EDGE,"E24.top");var subQ19=sQuery(id+"F5.wireOp",EDGE,"E24.bottom");var subQ20=sQuery(id+"F2.wireOp",EDGE,"E18");var subQ21=sQuery(id+"F2.wireOp",EDGE,"E17");var subQ22=sQuery(id+"F2.wireOp",EDGE,"E7.left");var subQ23=sQuery(id+"F2.wireOp",EDGE,"E7.top");var subQ24=sQuery(id+"F2.wireOp",EDGE,"E23");var subQ25=sQuery(id+"F2.wireOp",EDGE,"E22");var subQ26=sQuery(id+"F2.wireOp",EDGE,"E21");var subQ27=sQuery(id+"F2.wireOp",EDGE,"E20");var subQ28=sQuery(id+"F2.wireOp",EDGE,"E19");var subQ29=sQuery(id+"F2.wireOp",EDGE,"E16");var subQ30=sQuery(id+"F2.wireOp",EDGE,"E15");var subQ31=sQuery(id+"F2.wireOp",EDGE,"E14");var subQ32=sQuery(id+"F2.wireOp",EDGE,"E13.right");var subQ33=sQuery(id+"F2.wireOp",EDGE,"E13.left");var subQ34=sQuery(id+"F2.wireOp",EDGE,"E13.top");var subQ35=sQuery(id+"F2.wireOp",EDGE,"E11");var subQ36=sQuery(id+"F2.wireOp",EDGE,"E10");var subQ37=sQuery(id+"F2.wireOp",EDGE,"E9");var subQ38=sQuery(id+"F2.wireOp",EDGE,"E8");var subQ39=sQuery(id+"F2.wireOp",EDGE,"E7.right");var subQ40=sQuery(id+"F2.wireOp",EDGE,"E7.bottom");var subQ41=sQuery(id+"F2.wireOp",EDGE,"E6");var subQ42=sQuery(id+"F2.wireOp",EDGE,"E5.right");var subQ43=sQuery(id+"F2.wireOp",EDGE,"E5.left");var subQ44=sQuery(id+"F2.wireOp",EDGE,"E5.top");var subQ45=sQuery(id+"F2.wireOp",EDGE,"E5.bottom");var subQ46=sQuery(id+"F2.wireOp",EDGE,"E4.right");var subQ47=sQuery(id+"F2.wireOp",EDGE,"E4.top");var subQ48=sQuery(id+"F2.wireOp",EDGE,"E3.right");var subQ49=sQuery(id+"F2.wireOp",EDGE,"E3.left");var subQ50=sQuery(id+"F2.wireOp",EDGE,"E3.top");var subQ51=sQuery(id+"F2.wireOp",EDGE,"E3.bottom");var subQ52=sQuery(id+"F2.wireOp",EDGE,"E2.right");var subQ53=sQuery(id+"F2.wireOp",EDGE,"E2.left");var subQ54=sQuery(id+"F2.wireOp",EDGE,"E2.top");var subQ55=sQuery(id+"F2.wireOp",EDGE,"E2.bottom");var subQ56=sQuery(id+"F2.wireOp",EDGE,"E1.right");var subQ57=sQuery(id+"F2.wireOp",EDGE,"E1.left");var subQ58=sQuery(id+"F2.wireOp",EDGE,"E1.top");var subQ59=sQuery(id+"F2.wireOp",EDGE,"E1.bottom");var subQ60=makeQuery(id+"F6.boolean.opBoolean","MERGE",FACE,{"derivedFrom":[makeQuery(id+"F3.boolean.opBoolean","COPY",FACE,{"derivedFrom":makeQuery(id+"F3.opExtrude","CAP_FACE",FACE,{"disambiguationData":[OSD([subQ59,subQ58,subQ57,subQ56])],"isStart":false})}),makeQuery(id+"F3.boolean.opBoolean","COPY",FACE,{"derivedFrom":makeQuery(id+"F3.opExtrude","CAP_FACE",FACE,{"disambiguationData":[OSD([subQ55,subQ54,subQ53,subQ52])],"isStart":false})}),makeQuery(id+"F3.boolean.opBoolean","COPY",FACE,{"derivedFrom":makeQuery(id+"F3.opExtrude","CAP_FACE",FACE,{"disambiguationData":[OSD([subQ51,subQ50,subQ49,subQ48])],"isStart":false})}),makeQuery(id+"F3.boolean.opBoolean","COPY",FACE,{"derivedFrom":makeQuery(id+"F3.opExtrude","CAP_FACE",FACE,{"disambiguationData":[OSD([subQ0,subQ47,subQ2,subQ46])],"isStart":false})}),makeQuery(id+"F3.boolean.opBoolean","COPY",FACE,{"derivedFrom":makeQuery(id+"F3.opExtrude","CAP_FACE",FACE,{"disambiguationData":[OSD([subQ45,subQ44,subQ43,subQ42])],"isStart":false})}),makeQuery(id+"F3.boolean.opBoolean","COPY",FACE,{"derivedFrom":makeQuery(id+"F3.opExtrude","CAP_FACE",FACE,{"disambiguationData":[OSD([subQ41,subQ40,subQ39,subQ38,subQ37,subQ36,subQ35,subQ34,subQ33,subQ32,subQ31,subQ30,subQ29,subQ28,subQ27,subQ26,subQ25,subQ24])],"isStart":false})}),makeQuery(id+"F3.boolean.opBoolean","COPY",FACE,{"derivedFrom":makeQuery(id+"F3.opExtrude","CAP_FACE",FACE,{"disambiguationData":[OSD([subQ23,subQ22,subQ21,subQ20])],"isStart":false})}),makeQuery(id+"F6.opExtrude","CAP_FACE",FACE,{"disambiguationData":[OSD([subQ19,subQ18,sQuery(id+"F5.wireOp",EDGE,"E24.left"),sQuery(id+"F5.wireOp",EDGE,"E24.right")])],"isStart":true}),makeQuery(id+"F6.opExtrude","CAP_FACE",FACE,{"disambiguationData":[OSD([subQ17,subQ16,sQuery(id+"F5.wireOp",EDGE,"E25.left"),sQuery(id+"F5.wireOp",EDGE,"E25.right")])],"isStart":true}),makeQuery(id+"F6.opExtrude","CAP_FACE",FACE,{"disambiguationData":[OSD([subQ15,subQ14,sQuery(id+"F5.wireOp",EDGE,"E26.left"),sQuery(id+"F5.wireOp",EDGE,"E26.right")])],"isStart":true}),makeQuery(id+"F6.opExtrude","CAP_FACE",FACE,{"disambiguationData":[OSD([subQ13,subQ12,sQuery(id+"F5.wireOp",EDGE,"E27.left"),sQuery(id+"F5.wireOp",EDGE,"E27.right")])],"isStart":true}),makeQuery(id+"F6.opExtrude","CAP_FACE",FACE,{"disambiguationData":[OSD([sQuery(id+"F5.wireOp",EDGE,"E28.bottom"),sQuery(id+"F5.wireOp",EDGE,"E28.top"),subQ11,subQ10])],"isStart":true}),makeQuery(id+"F6.opExtrude","CAP_FACE",FACE,{"disambiguationData":[OSD([sQuery(id+"F5.wireOp",EDGE,"E29.bottom"),sQuery(id+"F5.wireOp",EDGE,"E29.top"),subQ9,subQ8])],"isStart":true}),makeQuery(id+"F6.opExtrude","CAP_FACE",FACE,{"disambiguationData":[OSD([subQ7,subQ6,sQuery(id+"F5.wireOp",EDGE,"E30.left"),sQuery(id+"F5.wireOp",EDGE,"E30.right")])],"isStart":true}),makeQuery(id+"F6.opExtrude","CAP_FACE",FACE,{"disambiguationData":[OSD([subQ5,subQ4,sQuery(id+"F5.wireOp",EDGE,"E31.left"),sQuery(id+"F5.wireOp",EDGE,"E31.right")])],"isStart":true})]});Q0=makeQuery(id+"F25.boolean.opBoolean","MERGE",FACE,{"derivedFrom":[makeQuery(id+"F19.boolean.opBoolean","MERGE",FACE,{"derivedFrom":[makeQuery(id+"F17.boolean.opBoolean","SPLIT",FACE,{"disambiguationData":[TD([makeQuery(id+"F1.opExtrude","SWEPT_FACE",FACE,{"disambiguationData":[OSD([sQuery(id+"F0.wireOp",EDGE,"E0.left")])]})])],"derivedFrom":subQ60}),makeQuery(id+"F17.boolean.opBoolean","SPLIT",FACE,{"disambiguationData":[TD([makeQuery(id+"F17.opExtrude","SWEPT_FACE",FACE,{"disambiguationData":[OSD([sQuery(id+"F16.wireOp",EDGE,"E69")])]})])],"derivedFrom":subQ60}),makeQuery(id+"F19.opExtrude","CAP_FACE",FACE,{"disambiguationData":[OSD([sQuery(id+"F18.wireOp",EDGE,"E73.bottom"),sQuery(id+"F18.wireOp",EDGE,"E73.top"),sQuery(id+"F18.wireOp",EDGE,"E73.left"),sQuery(id+"F18.wireOp",EDGE,"E73.right")])],"isStart":true})]}),makeQuery(id+"F25.opExtrude","CAP_FACE",FACE,{"disambiguationData":[OSD([sQuery(id+"F24.wireOp",EDGE,"E90.bottom"),sQuery(id+"F24.wireOp",EDGE,"E90.top"),sQuery(id+"F24.wireOp",EDGE,"E90.left"),sQuery(id+"F24.wireOp",EDGE,"E90.right")])],"isStart":true})]});}
            var sketch = newSketch(context, id + "F26", { "sketchPlane" : qUnion([Q0])});
            skArc(sketch, "E91", {"start": v(-5.3, 38.52) * mm, "mid": v(-7.15, 34.03) * mm, "end": v(-11.64, 32.17) * mm});
            skArc(sketch, "E92", {"start": v(-5.42, 38.52) * mm, "mid": v(-7.24, 34.12) * mm, "end": v(-11.64, 32.3) * mm});
            skLineSegment(sketch, "E93", {"start": v(-11.64, 32.17) * mm, "end": v(-11.64, 32.3) * mm});
            skLineSegment(sketch, "E94", {"start": v(-5.42, 38.52) * mm, "end": v(-5.3, 38.52) * mm});
            skSolve(sketch);
        }
        {
            var Q0;
            Q0 = qSketchRegion(id + "F26", true);
            extrude(context, id + "F27", {"entities" : qUnion([Q0]), "operationType" : NewBodyOperationType.REMOVE, "oppositeDirection" : true, "depth" : 0.25 * mm});
        }
        {
            var Q0;
            {var subQ33=sQuery(id+"F16.wireOp",EDGE,"E68");var subQ36=sQuery(id+"F16.wireOp",EDGE,"E67");var subQ42=sQuery(id+"F0.wireOp",EDGE,"E0.bottom");var subQ43=makeQuery(id+"F1.opExtrude","SWEPT_FACE",FACE,{"disambiguationData":[OSD([subQ42])]});var subQ55=sQuery(id+"F0.wireOp",EDGE,"E0.right");var subQ57=sQuery(id+"F9.wireOp",EDGE,"E61.bottom");var subQ63=sQuery(id+"F0.wireOp",EDGE,"E0.top");var subQ64=makeQuery(id+"F1.opExtrude","SWEPT_FACE",FACE,{"disambiguationData":[OSD([subQ63])]});var subQ69=sQuery(id+"F0.wireOp",EDGE,"E0.left");var subQ73=sQuery(id+"F16.wireOp",EDGE,"E69");var subQ75=sQuery(id+"F16.wireOp",EDGE,"E70");var subQ85=sQuery(id+"F9.wireOp",EDGE,"E63");Q0=makeQuery(id+"F25.boolean.opBoolean","SPLIT",FACE,{"disambiguationData":[TD([subQ64])],"derivedFrom":makeQuery(id+"F17.boolean.opBoolean","MERGE",FACE,{"derivedFrom":[makeQuery(id+"F15.boolean.opBoolean","SPLIT",FACE,{"disambiguationData":[TD([subQ43])],"derivedFrom":makeQuery(id+"F11.boolean.opBoolean","MERGE",FACE,{"derivedFrom":[makeQuery(id+"F6.boolean.opBoolean","SPLIT",FACE,{"disambiguationData":[TD([subQ43])],"derivedFrom":makeQuery(id+"F1.opExtrude","CAP_FACE",FACE,{"disambiguationData":[OSD([subQ42,subQ63,subQ69,subQ55])],"isStart":false})}),makeQuery(id+"F11.opExtrude","CAP_FACE",FACE,{"disambiguationData":[OSD([subQ57,sQuery(id+"F9.wireOp",EDGE,"E61.top"),sQuery(id+"F9.wireOp",EDGE,"E61.left"),subQ85])],"isStart":false})]})}),makeQuery(id+"F17.opExtrude","CAP_FACE",FACE,{"disambiguationData":[OSD([subQ36,subQ33,subQ73,subQ75,sQuery(id+"F16.wireOp",EDGE,"E71"),sQuery(id+"F16.wireOp",EDGE,"E72")])],"isStart":false})]})});}
            var sketch = newSketch(context, id + "F28", { "sketchPlane" : qUnion([Q0])});
            skLineSegment(sketch, "E95.bottom", {"start": v(-25.61, -40.15) * mm, "end": v(-20.74, -40.15) * mm});
            skLineSegment(sketch, "E95.top", {"start": v(-25.61, -37.72) * mm, "end": v(-20.74, -37.72) * mm});
            skLineSegment(sketch, "E95.left", {"start": v(-25.61, -40.15) * mm, "end": v(-25.61, -37.72) * mm});
            skLineSegment(sketch, "E95.right", {"start": v(-20.74, -40.15) * mm, "end": v(-20.74, -37.72) * mm});
            skLineSegment(sketch, "E96.bottom", {"start": v(-20.32, -37.83) * mm, "end": v(-15.45, -37.83) * mm});
            skLineSegment(sketch, "E96.top", {"start": v(-20.32, -40.54) * mm, "end": v(-15.45, -40.54) * mm});
            skLineSegment(sketch, "E96.left", {"start": v(-20.32, -37.83) * mm, "end": v(-20.32, -40.54) * mm});
            skLineSegment(sketch, "E96.right", {"start": v(-15.45, -37.83) * mm, "end": v(-15.45, -40.54) * mm});
            skSolve(sketch);
        }
        {
            var Q0;
            Q0 = qSketchRegion(id + "F28", true);
            extrude(context, id + "F29", {"entities" : qUnion([Q0]), "operationType" : NewBodyOperationType.REMOVE, "oppositeDirection" : true, "depth" : 2.54 * mm});
        }
        {
            var Q0;
            {var subQ0=sQuery(id+"F2.wireOp",EDGE,"E4.bottom");var subQ2=sQuery(id+"F2.wireOp",EDGE,"E4.left");var subQ4=sQuery(id+"F5.wireOp",EDGE,"E31.top");var subQ5=sQuery(id+"F5.wireOp",EDGE,"E31.bottom");var subQ6=sQuery(id+"F5.wireOp",EDGE,"E30.top");var subQ7=sQuery(id+"F5.wireOp",EDGE,"E30.bottom");var subQ8=sQuery(id+"F5.wireOp",EDGE,"E29.right");var subQ9=sQuery(id+"F5.wireOp",EDGE,"E29.left");var subQ10=sQuery(id+"F5.wireOp",EDGE,"E28.right");var subQ11=sQuery(id+"F5.wireOp",EDGE,"E28.left");var subQ12=sQuery(id+"F5.wireOp",EDGE,"E27.top");var subQ13=sQuery(id+"F5.wireOp",EDGE,"E27.bottom");var subQ14=sQuery(id+"F5.wireOp",EDGE,"E26.top");var subQ15=sQuery(id+"F5.wireOp",EDGE,"E26.bottom");var subQ16=sQuery(id+"F5.wireOp",EDGE,"E25.top");var subQ17=sQuery(id+"F5.wireOp",EDGE,"E25.bottom");var subQ18=sQuery(id+"F5.wireOp",EDGE,"E24.top");var subQ19=sQuery(id+"F5.wireOp",EDGE,"E24.bottom");var subQ20=sQuery(id+"F2.wireOp",EDGE,"E18");var subQ21=sQuery(id+"F2.wireOp",EDGE,"E17");var subQ22=sQuery(id+"F2.wireOp",EDGE,"E7.left");var subQ23=sQuery(id+"F2.wireOp",EDGE,"E7.top");var subQ24=sQuery(id+"F2.wireOp",EDGE,"E23");var subQ25=sQuery(id+"F2.wireOp",EDGE,"E22");var subQ26=sQuery(id+"F2.wireOp",EDGE,"E21");var subQ27=sQuery(id+"F2.wireOp",EDGE,"E20");var subQ28=sQuery(id+"F2.wireOp",EDGE,"E19");var subQ29=sQuery(id+"F2.wireOp",EDGE,"E16");var subQ30=sQuery(id+"F2.wireOp",EDGE,"E15");var subQ31=sQuery(id+"F2.wireOp",EDGE,"E14");var subQ32=sQuery(id+"F2.wireOp",EDGE,"E13.right");var subQ33=sQuery(id+"F2.wireOp",EDGE,"E13.left");var subQ34=sQuery(id+"F2.wireOp",EDGE,"E13.top");var subQ35=sQuery(id+"F2.wireOp",EDGE,"E11");var subQ36=sQuery(id+"F2.wireOp",EDGE,"E10");var subQ37=sQuery(id+"F2.wireOp",EDGE,"E9");var subQ38=sQuery(id+"F2.wireOp",EDGE,"E8");var subQ39=sQuery(id+"F2.wireOp",EDGE,"E7.right");var subQ40=sQuery(id+"F2.wireOp",EDGE,"E7.bottom");var subQ41=sQuery(id+"F2.wireOp",EDGE,"E6");var subQ42=sQuery(id+"F2.wireOp",EDGE,"E5.right");var subQ43=sQuery(id+"F2.wireOp",EDGE,"E5.left");var subQ44=sQuery(id+"F2.wireOp",EDGE,"E5.top");var subQ45=sQuery(id+"F2.wireOp",EDGE,"E5.bottom");var subQ46=sQuery(id+"F2.wireOp",EDGE,"E4.right");var subQ47=sQuery(id+"F2.wireOp",EDGE,"E4.top");var subQ48=sQuery(id+"F2.wireOp",EDGE,"E3.right");var subQ49=sQuery(id+"F2.wireOp",EDGE,"E3.left");var subQ50=sQuery(id+"F2.wireOp",EDGE,"E3.top");var subQ51=sQuery(id+"F2.wireOp",EDGE,"E3.bottom");var subQ52=sQuery(id+"F2.wireOp",EDGE,"E2.right");var subQ53=sQuery(id+"F2.wireOp",EDGE,"E2.left");var subQ54=sQuery(id+"F2.wireOp",EDGE,"E2.top");var subQ55=sQuery(id+"F2.wireOp",EDGE,"E2.bottom");var subQ56=sQuery(id+"F2.wireOp",EDGE,"E1.right");var subQ57=sQuery(id+"F2.wireOp",EDGE,"E1.left");var subQ58=sQuery(id+"F2.wireOp",EDGE,"E1.top");var subQ59=sQuery(id+"F2.wireOp",EDGE,"E1.bottom");var subQ60=makeQuery(id+"F6.boolean.opBoolean","MERGE",FACE,{"derivedFrom":[makeQuery(id+"F3.boolean.opBoolean","COPY",FACE,{"derivedFrom":makeQuery(id+"F3.opExtrude","CAP_FACE",FACE,{"disambiguationData":[OSD([subQ59,subQ58,subQ57,subQ56])],"isStart":false})}),makeQuery(id+"F3.boolean.opBoolean","COPY",FACE,{"derivedFrom":makeQuery(id+"F3.opExtrude","CAP_FACE",FACE,{"disambiguationData":[OSD([subQ55,subQ54,subQ53,subQ52])],"isStart":false})}),makeQuery(id+"F3.boolean.opBoolean","COPY",FACE,{"derivedFrom":makeQuery(id+"F3.opExtrude","CAP_FACE",FACE,{"disambiguationData":[OSD([subQ51,subQ50,subQ49,subQ48])],"isStart":false})}),makeQuery(id+"F3.boolean.opBoolean","COPY",FACE,{"derivedFrom":makeQuery(id+"F3.opExtrude","CAP_FACE",FACE,{"disambiguationData":[OSD([subQ0,subQ47,subQ2,subQ46])],"isStart":false})}),makeQuery(id+"F3.boolean.opBoolean","COPY",FACE,{"derivedFrom":makeQuery(id+"F3.opExtrude","CAP_FACE",FACE,{"disambiguationData":[OSD([subQ45,subQ44,subQ43,subQ42])],"isStart":false})}),makeQuery(id+"F3.boolean.opBoolean","COPY",FACE,{"derivedFrom":makeQuery(id+"F3.opExtrude","CAP_FACE",FACE,{"disambiguationData":[OSD([subQ41,subQ40,subQ39,subQ38,subQ37,subQ36,subQ35,subQ34,subQ33,subQ32,subQ31,subQ30,subQ29,subQ28,subQ27,subQ26,subQ25,subQ24])],"isStart":false})}),makeQuery(id+"F3.boolean.opBoolean","COPY",FACE,{"derivedFrom":makeQuery(id+"F3.opExtrude","CAP_FACE",FACE,{"disambiguationData":[OSD([subQ23,subQ22,subQ21,subQ20])],"isStart":false})}),makeQuery(id+"F6.opExtrude","CAP_FACE",FACE,{"disambiguationData":[OSD([subQ19,subQ18,sQuery(id+"F5.wireOp",EDGE,"E24.left"),sQuery(id+"F5.wireOp",EDGE,"E24.right")])],"isStart":true}),makeQuery(id+"F6.opExtrude","CAP_FACE",FACE,{"disambiguationData":[OSD([subQ17,subQ16,sQuery(id+"F5.wireOp",EDGE,"E25.left"),sQuery(id+"F5.wireOp",EDGE,"E25.right")])],"isStart":true}),makeQuery(id+"F6.opExtrude","CAP_FACE",FACE,{"disambiguationData":[OSD([subQ15,subQ14,sQuery(id+"F5.wireOp",EDGE,"E26.left"),sQuery(id+"F5.wireOp",EDGE,"E26.right")])],"isStart":true}),makeQuery(id+"F6.opExtrude","CAP_FACE",FACE,{"disambiguationData":[OSD([subQ13,subQ12,sQuery(id+"F5.wireOp",EDGE,"E27.left"),sQuery(id+"F5.wireOp",EDGE,"E27.right")])],"isStart":true}),makeQuery(id+"F6.opExtrude","CAP_FACE",FACE,{"disambiguationData":[OSD([sQuery(id+"F5.wireOp",EDGE,"E28.bottom"),sQuery(id+"F5.wireOp",EDGE,"E28.top"),subQ11,subQ10])],"isStart":true}),makeQuery(id+"F6.opExtrude","CAP_FACE",FACE,{"disambiguationData":[OSD([sQuery(id+"F5.wireOp",EDGE,"E29.bottom"),sQuery(id+"F5.wireOp",EDGE,"E29.top"),subQ9,subQ8])],"isStart":true}),makeQuery(id+"F6.opExtrude","CAP_FACE",FACE,{"disambiguationData":[OSD([subQ7,subQ6,sQuery(id+"F5.wireOp",EDGE,"E30.left"),sQuery(id+"F5.wireOp",EDGE,"E30.right")])],"isStart":true}),makeQuery(id+"F6.opExtrude","CAP_FACE",FACE,{"disambiguationData":[OSD([subQ5,subQ4,sQuery(id+"F5.wireOp",EDGE,"E31.left"),sQuery(id+"F5.wireOp",EDGE,"E31.right")])],"isStart":true})]});Q0=makeQuery(id+"F25.boolean.opBoolean","MERGE",FACE,{"derivedFrom":[makeQuery(id+"F19.boolean.opBoolean","MERGE",FACE,{"derivedFrom":[makeQuery(id+"F17.boolean.opBoolean","SPLIT",FACE,{"disambiguationData":[TD([makeQuery(id+"F1.opExtrude","SWEPT_FACE",FACE,{"disambiguationData":[OSD([sQuery(id+"F0.wireOp",EDGE,"E0.left")])]})])],"derivedFrom":subQ60}),makeQuery(id+"F17.boolean.opBoolean","SPLIT",FACE,{"disambiguationData":[TD([makeQuery(id+"F17.opExtrude","SWEPT_FACE",FACE,{"disambiguationData":[OSD([sQuery(id+"F16.wireOp",EDGE,"E69")])]})])],"derivedFrom":subQ60}),makeQuery(id+"F19.opExtrude","CAP_FACE",FACE,{"disambiguationData":[OSD([sQuery(id+"F18.wireOp",EDGE,"E73.bottom"),sQuery(id+"F18.wireOp",EDGE,"E73.top"),sQuery(id+"F18.wireOp",EDGE,"E73.left"),sQuery(id+"F18.wireOp",EDGE,"E73.right")])],"isStart":true})]}),makeQuery(id+"F25.opExtrude","CAP_FACE",FACE,{"disambiguationData":[OSD([sQuery(id+"F24.wireOp",EDGE,"E90.bottom"),sQuery(id+"F24.wireOp",EDGE,"E90.top"),sQuery(id+"F24.wireOp",EDGE,"E90.left"),sQuery(id+"F24.wireOp",EDGE,"E90.right")])],"isStart":true})]});}
            var sketch = newSketch(context, id + "F30", { "sketchPlane" : qUnion([Q0])});
            skLineSegment(sketch, "E97.bottom", {"start": v(-12.91, 38.52) * mm, "end": v(-15.45, 38.52) * mm});
            skLineSegment(sketch, "E97.top", {"start": v(-12.91, 35.98) * mm, "end": v(-15.45, 35.98) * mm});
            skLineSegment(sketch, "E97.left", {"start": v(-12.91, 38.52) * mm, "end": v(-12.91, 35.98) * mm});
            skLineSegment(sketch, "E97.right", {"start": v(-15.45, 38.52) * mm, "end": v(-15.45, 35.98) * mm});
            skLineSegment(sketch, "E98", {"start": v(-15.24, 38.52) * mm, "end": v(-15.24, 36.2) * mm});
            skLineSegment(sketch, "E99", {"start": v(-15.24, 36.2) * mm, "end": v(-12.91, 36.2) * mm});
            skCircle(sketch, "E100", {"center": v(-14.08, 37.36) * mm, "radius": 0.32 * mm});
            skPoint(sketch, "E100.centerSnap0", {"position": v(-14.08, 36.2) * mm});
            skPoint(sketch, "E100.centerSnap1", {"position": v(-15.24, 37.36) * mm});
            skSolve(sketch);
        }
        {
            var Q0;
            Q0=makeQuery(id+"F30.imprint","IMPRINT",FACE,{"disambiguationData":[TD([[makeQuery(id+"F30.imprint","IMPRINT",EDGE,{"derivedFrom":sQuery(id+"F30.wireOp",EDGE,"E100")}),1.0]])]});
            var Q1;
            {var subQ1=sQuery(id+"F30.wireOp",EDGE,"E97.top");Q1=makeQuery(id+"F30.imprint","IMPRINT",FACE,{"disambiguationData":[TD([[makeQuery(id+"F30.imprint","IMPRINT",EDGE,{"derivedFrom":subQ1}),-1.0]])]});}
            extrude(context, id + "F31", {"entities" : qUnion([Q0, Q1]), "operationType" : NewBodyOperationType.ADD, "depth" : 19.05 * mm});
        }
    });
